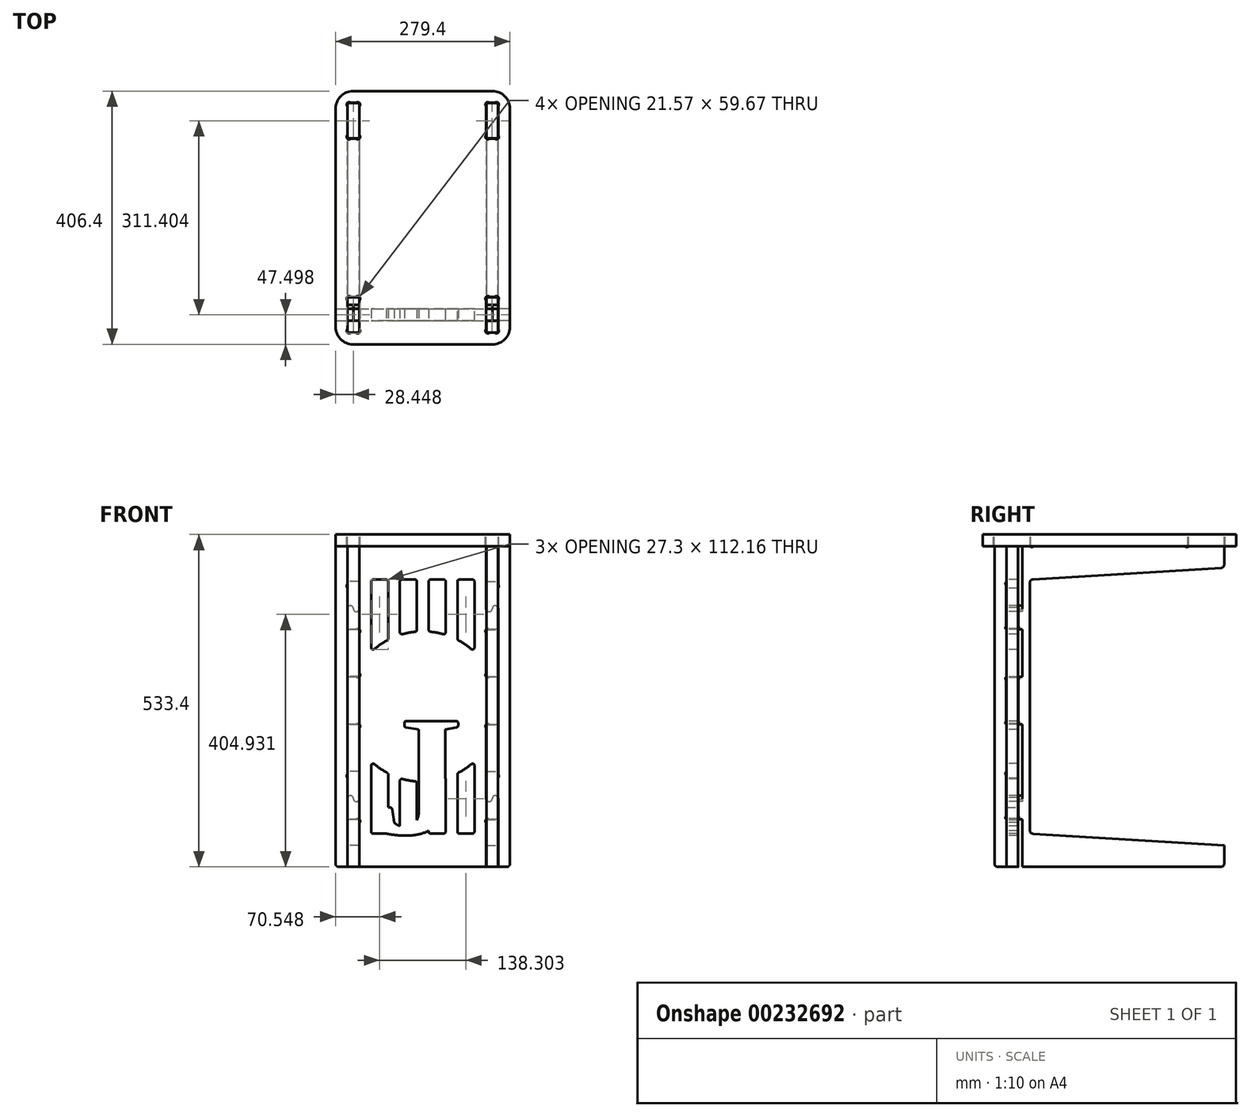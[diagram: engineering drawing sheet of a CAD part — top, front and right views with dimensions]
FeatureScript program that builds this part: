
annotation { "Feature Type Name" : "Feature", "Feature Type Description" : "" }
export const myFeature = defineFeature(function(context is Context, id is Id, definition is map)
    precondition{}
    {
        {
            assignVariable(context, id + "F0", {"name" : "table_width", "anyValue" : 279.4 * mm});
        }
        {
            assignVariable(context, id + "F1", {"name" : "material_thickness", "anyValue" : 18.8 * mm});
        }
        {
            assignVariable(context, id + "F2", {"name" : "material_clearance", "anyValue" : 0.25 * mm});
        }
        {
            assignVariable(context, id + "F3", {"name" : "tool_diameter", "anyValue" : 6.35 * mm});
        }
        {
            assignVariable(context, id + "F4", {"name" : "large_fillet_radius", "anyValue" : 0.1 * getVariable(context, 'table_width')});
        }
        {
            assignVariable(context, id + "F5", {"name" : "small_fillet_radius", "anyValue" : 0.25 * getVariable(context, 'material_thickness')});
        }
        {
            assignVariable(context, id + "F6", {"name" : "tabs_fillet_radius", "anyValue" : 0.1 * getVariable(context, 'material_thickness')});
        }
        {
            var Q0;
            Q0=qCreatedBy(makeId("Right.planeOp"),FACE);
            cPlane(context, id + "F7", {"entities" : qUnion([Q0]), "cplaneType" : CPlaneType.OFFSET, "offset" : getVariable(context, 'table_width') / 2 - getVariable(context, 'material_thickness') - getVariable(context, 'material_clearance'), "oppositeDirection" : true, "width" : 152.4 * mm, "height" : 152.4 * mm});
        }
        {
            var Q0;
            Q0=qCreatedBy(id+"F7.planeOp",FACE);
            var sketch = newSketch(context, id + "F8", { "sketchPlane" : qUnion([Q0])});
            skLineSegment(sketch, "E0.bottom", {"start": v(368.3, 0) * mm, "end": v(0, 0) * mm});
            skLineSegment(sketch, "E0.top", {"start": v(368.3, -533.4) * mm, "end": v(0, -533.4) * mm});
            skLineSegment(sketch, "E0.left", {"start": v(368.3, 0) * mm, "end": v(368.3, -533.4) * mm});
            skLineSegment(sketch, "E0.right", {"start": v(0, 0) * mm, "end": v(0, -533.4) * mm});
            skSolve(sketch);
        }
        {
            var Q0;
            Q0 = qSketchRegion(id + "F8", true);
            extrude(context, id + "F9", {"entities" : qUnion([Q0]), "depth" : getVariable(context, 'material_thickness')});
        }
        {
            var Q0;
            Q0=makeQuery(id+"F9.opExtrude","CAP_FACE",FACE,{"disambiguationData":[OSD([sQuery(id+"F8.wireOp",EDGE,"E0.bottom"),sQuery(id+"F8.wireOp",EDGE,"E0.top"),sQuery(id+"F8.wireOp",EDGE,"E0.left"),sQuery(id+"F8.wireOp",EDGE,"E0.right")])],"isStart":true});
            var sketch = newSketch(context, id + "F10", { "sketchPlane" : qUnion([Q0])});
            skLineSegment(sketch, "E1", {"start": v(-368.3, -53.34) * mm, "end": v(-56.9, -72.4) * mm});
            skLineSegment(sketch, "E2", {"start": v(-56.9, -72.4) * mm, "end": v(-56.9, -480.06) * mm});
            skLineSegment(sketch, "E3", {"start": v(-56.9, -480.06) * mm, "end": v(-368.3, -499.1) * mm});
            skLineSegment(sketch, "E4", {"start": v(-368.3, -499.1) * mm, "end": v(-368.3, -53.34) * mm});
            skLineSegment(sketch, "E5", {"start": v(-56.9, -72.4) * mm, "end": v(-368.3, -72.39) * mm, "construction": true});
            skLineSegment(sketch, "E6", {"start": v(-56.9, -480.06) * mm, "end": v(-368.3, -480.06) * mm, "construction": true});
            skLineSegment(sketch, "E7.bottom", {"start": v(-311.4, 0) * mm, "end": v(-56.9, 0) * mm});
            skLineSegment(sketch, "E7.top", {"start": v(-311.4, -19.05) * mm, "end": v(-56.9, -19.05) * mm});
            skLineSegment(sketch, "E7.left", {"start": v(-311.4, 0) * mm, "end": v(-311.4, -19.05) * mm});
            skLineSegment(sketch, "E7.right", {"start": v(-56.9, 0) * mm, "end": v(-56.9, -19.05) * mm});
            skLineSegment(sketch, "E8.bottom", {"start": v(-38.1, -75.95) * mm, "end": v(-18.8, -75.95) * mm});
            skLineSegment(sketch, "E8.top", {"start": v(-38.1, -152.65) * mm, "end": v(-18.8, -152.65) * mm});
            skLineSegment(sketch, "E8.left", {"start": v(-38.1, -75.95) * mm, "end": v(-38.1, -152.65) * mm});
            skLineSegment(sketch, "E8.right", {"start": v(-18.8, -75.95) * mm, "end": v(-18.8, -152.65) * mm});
            skLineSegment(sketch, "E9.0.1.0", {"start": v(-38.1, -305.05) * mm, "end": v(-18.8, -305.05) * mm});
            skLineSegment(sketch, "E9.0.1.1", {"start": v(-18.8, -228.35) * mm, "end": v(-18.8, -305.05) * mm});
            skLineSegment(sketch, "E9.0.1.2", {"start": v(-38.1, -228.35) * mm, "end": v(-38.1, -305.05) * mm});
            skLineSegment(sketch, "E9.0.1.3", {"start": v(-38.1, -228.35) * mm, "end": v(-18.8, -228.35) * mm});
            skLineSegment(sketch, "E9.0.2.0", {"start": v(-38.1, -457.45) * mm, "end": v(-18.8, -457.45) * mm});
            skLineSegment(sketch, "E9.0.2.1", {"start": v(-18.8, -380.75) * mm, "end": v(-18.8, -457.45) * mm});
            skLineSegment(sketch, "E9.0.2.2", {"start": v(-38.1, -380.75) * mm, "end": v(-38.1, -457.45) * mm});
            skLineSegment(sketch, "E9.0.2.3", {"start": v(-38.1, -380.75) * mm, "end": v(-18.8, -380.75) * mm});
            skLineSegment(sketch, "E9.direction1", {"start": v(-38.1, -152.65) * mm, "end": v(7.11, -152.65) * mm, "construction": true});
            skLineSegment(sketch, "E9.direction2", {"start": v(-38.1, -152.65) * mm, "end": v(-38.1, -305.05) * mm, "construction": true});
            skSolve(sketch);
        }
        {
            var Q0;
            Q0 = qSketchRegion(id + "F10", true);
            extrude(context, id + "F11", {"entities" : qUnion([Q0]), "operationType" : NewBodyOperationType.REMOVE, "oppositeDirection" : true, "depth" : getVariable(context, 'material_thickness')});
        }
        {
            var Q0;
            Q0=makeQuery(id+"F11.boolean.opBoolean","COPY",EDGE,{"derivedFrom":makeQuery(id+"F11.opExtrude","SWEPT_EDGE",EDGE,{"disambiguationData":[OSD([sQuery(id+"F8.wireOp",EDGE,"E0.left"),sQuery(id+"F10.wireOp",EDGE,"E1"),sQuery(id+"F10.wireOp",EDGE,"E4")])]})});
            var Q1;
            Q1=makeQuery(id+"F11.boolean.opBoolean","COPY",EDGE,{"derivedFrom":makeQuery(id+"F11.opExtrude","SWEPT_EDGE",EDGE,{"disambiguationData":[OSD([sQuery(id+"F10.wireOp",EDGE,"E1"),sQuery(id+"F10.wireOp",EDGE,"E2")])]})});
            var Q2;
            Q2=makeQuery(id+"F11.boolean.opBoolean","COPY",EDGE,{"derivedFrom":makeQuery(id+"F11.opExtrude","SWEPT_EDGE",EDGE,{"disambiguationData":[OSD([sQuery(id+"F10.wireOp",EDGE,"E2"),sQuery(id+"F10.wireOp",EDGE,"E3")])]})});
            var Q3;
            Q3=makeQuery(id+"F11.boolean.opBoolean","COPY",EDGE,{"derivedFrom":makeQuery(id+"F11.opExtrude","SWEPT_EDGE",EDGE,{"disambiguationData":[OSD([sQuery(id+"F8.wireOp",EDGE,"E0.left"),sQuery(id+"F10.wireOp",EDGE,"E3"),sQuery(id+"F10.wireOp",EDGE,"E4")])]})});
            var Q4;
            Q4=makeQuery(id+"F9.opExtrude","SWEPT_EDGE",EDGE,{"disambiguationData":[OSD([sQuery(id+"F8.wireOp",EDGE,"E0.top"),sQuery(id+"F8.wireOp",EDGE,"E0.left")])]});
            var Q5;
            Q5=makeQuery(id+"F9.opExtrude","SWEPT_EDGE",EDGE,{"disambiguationData":[OSD([sQuery(id+"F8.wireOp",EDGE,"E0.top"),sQuery(id+"F8.wireOp",EDGE,"E0.right")])]});
            fillet(context, id + "F12", {"entities" : qUnion([Q0, Q1, Q2, Q3, Q4, Q5]), "radius" : 5.08 * mm, "tangentPropagation" : true, "allowEdgeOverflow" : false});
        }
        {
            var Q0;
            Q0=makeQuery(id+"F9.opExtrude","SWEPT_EDGE",EDGE,{"disambiguationData":[OSD([sQuery(id+"F8.wireOp",EDGE,"E0.bottom"),sQuery(id+"F8.wireOp",EDGE,"E0.left")])]});
            var Q1;
            Q1=makeQuery(id+"F11.boolean.opBoolean","COPY",EDGE,{"derivedFrom":makeQuery(id+"F11.opExtrude","SWEPT_EDGE",EDGE,{"disambiguationData":[OSD([sQuery(id+"F8.wireOp",EDGE,"E0.bottom"),sQuery(id+"F10.wireOp",EDGE,"E7.bottom"),sQuery(id+"F10.wireOp",EDGE,"E7.left")])]})});
            var Q2;
            Q2=makeQuery(id+"F11.boolean.opBoolean","COPY",EDGE,{"derivedFrom":makeQuery(id+"F11.opExtrude","SWEPT_EDGE",EDGE,{"disambiguationData":[OSD([sQuery(id+"F8.wireOp",EDGE,"E0.bottom"),sQuery(id+"F10.wireOp",EDGE,"E7.bottom"),sQuery(id+"F10.wireOp",EDGE,"E7.right")])]})});
            var Q3;
            Q3=makeQuery(id+"F9.opExtrude","SWEPT_EDGE",EDGE,{"disambiguationData":[OSD([sQuery(id+"F8.wireOp",EDGE,"E0.bottom"),sQuery(id+"F8.wireOp",EDGE,"E0.right")])]});
            fillet(context, id + "F13", {"entities" : qUnion([Q0, Q1, Q2, Q3]), "radius" : getVariable(context, 'tabs_fillet_radius'), "tangentPropagation" : true, "allowEdgeOverflow" : false});
        }
        {
            var Q0;
            Q0=makeQuery(id+"F9.opExtrude","CAP_FACE",FACE,{"disambiguationData":[OSD([sQuery(id+"F8.wireOp",EDGE,"E0.bottom"),sQuery(id+"F8.wireOp",EDGE,"E0.top"),sQuery(id+"F8.wireOp",EDGE,"E0.left"),sQuery(id+"F8.wireOp",EDGE,"E0.right")])],"isStart":true});
            var sketch = newSketch(context, id + "F14", { "sketchPlane" : qUnion([Q0])});
            skArc(sketch, "E10", {"start": v(-311.99, -14.18) * mm, "mid": v(-311.4, -19.05) * mm, "end": v(-306.53, -19.63) * mm});
            skArc(sketch, "E11", {"start": v(-306.53, -19.63) * mm, "mid": v(-305.54, -19.2) * mm, "end": v(-304.46, -19.05) * mm});
            skArc(sketch, "E12", {"start": v(-311.99, -14.18) * mm, "mid": v(-311.55, -13.18) * mm, "end": v(-311.4, -12.1) * mm});
            skLineSegment(sketch, "E13", {"start": v(-308.6, -16.24) * mm, "end": v(-311.4, -19.05) * mm, "construction": true});
            skLineSegment(sketch, "E14", {"start": v(-184.15, -19.05) * mm, "end": v(-184.15, -64.6) * mm, "construction": true});
            skArc(sketch, "E15.MirrorCS", {"start": v(-56.31, -14.18) * mm, "mid": v(-56.75, -13.18) * mm, "end": v(-56.9, -12.1) * mm});
            skArc(sketch, "E16.MirrorCS", {"start": v(-56.31, -14.18) * mm, "mid": v(-56.9, -19.05) * mm, "end": v(-61.77, -19.63) * mm});
            skArc(sketch, "E17.MirrorCS", {"start": v(-61.77, -19.63) * mm, "mid": v(-62.76, -19.2) * mm, "end": v(-63.84, -19.05) * mm});
            skLineSegment(sketch, "E18", {"start": v(-311.4, -12.1) * mm, "end": v(-304.46, -19.05) * mm});
            skLineSegment(sketch, "E19.MirrorCS", {"start": v(-56.9, -12.1) * mm, "end": v(-63.84, -19.05) * mm});
            skLineSegment(sketch, "E20", {"start": v(-38.1, -114.3) * mm, "end": v(-18.8, -114.3) * mm, "construction": true});
            skLineSegment(sketch, "E21", {"start": v(-28.45, -75.95) * mm, "end": v(-28.45, -152.65) * mm, "construction": true});
            skArc(sketch, "E22", {"start": v(-33.23, -75.36) * mm, "mid": v(-38.1, -75.95) * mm, "end": v(-38.68, -80.82) * mm});
            skArc(sketch, "E23", {"start": v(-33.23, -75.36) * mm, "mid": v(-32.23, -75.8) * mm, "end": v(-31.16, -75.95) * mm});
            skArc(sketch, "E24", {"start": v(-38.68, -80.82) * mm, "mid": v(-38.25, -81.81) * mm, "end": v(-38.1, -82.89) * mm});
            skLineSegment(sketch, "E25", {"start": v(-35.3, -78.75) * mm, "end": v(-38.1, -75.95) * mm, "construction": true});
            skLineSegment(sketch, "E26", {"start": v(-38.1, -82.89) * mm, "end": v(-31.16, -75.95) * mm});
            skLineSegment(sketch, "E27.MirrorCS", {"start": v(-18.8, -82.89) * mm, "end": v(-25.74, -75.95) * mm});
            skArc(sketch, "E28.MirrorCS", {"start": v(-23.67, -75.36) * mm, "mid": v(-24.66, -75.8) * mm, "end": v(-25.74, -75.95) * mm});
            skArc(sketch, "E29.MirrorCS", {"start": v(-23.67, -75.36) * mm, "mid": v(-18.8, -75.95) * mm, "end": v(-18.21, -80.82) * mm});
            skArc(sketch, "E30.MirrorCS", {"start": v(-18.21, -80.82) * mm, "mid": v(-18.65, -81.81) * mm, "end": v(-18.8, -82.89) * mm});
            skLineSegment(sketch, "E31.MirrorCS", {"start": v(-38.1, -145.71) * mm, "end": v(-31.16, -152.65) * mm});
            skArc(sketch, "E32.MirrorCS", {"start": v(-38.68, -147.78) * mm, "mid": v(-38.25, -146.79) * mm, "end": v(-38.1, -145.71) * mm});
            skArc(sketch, "E33.MirrorCS", {"start": v(-33.23, -153.24) * mm, "mid": v(-38.1, -152.65) * mm, "end": v(-38.68, -147.78) * mm});
            skArc(sketch, "E34.MirrorCS", {"start": v(-33.23, -153.24) * mm, "mid": v(-32.23, -152.8) * mm, "end": v(-31.16, -152.65) * mm});
            skLineSegment(sketch, "E35.MirrorCS", {"start": v(-18.8, -145.71) * mm, "end": v(-25.74, -152.65) * mm});
            skArc(sketch, "E36.MirrorCS", {"start": v(-23.67, -153.24) * mm, "mid": v(-24.66, -152.8) * mm, "end": v(-25.74, -152.65) * mm});
            skArc(sketch, "E37.MirrorCS", {"start": v(-23.67, -153.24) * mm, "mid": v(-18.8, -152.65) * mm, "end": v(-18.21, -147.78) * mm});
            skArc(sketch, "E38.MirrorCS", {"start": v(-18.21, -147.78) * mm, "mid": v(-18.65, -146.79) * mm, "end": v(-18.8, -145.71) * mm});
            skArc(sketch, "E39.0.1.0", {"start": v(-38.68, -300.18) * mm, "mid": v(-38.25, -299.19) * mm, "end": v(-38.1, -298.11) * mm});
            skArc(sketch, "E39.0.1.1", {"start": v(-33.23, -305.64) * mm, "mid": v(-38.1, -305.05) * mm, "end": v(-38.68, -300.18) * mm});
            skArc(sketch, "E39.0.1.2", {"start": v(-33.23, -305.64) * mm, "mid": v(-32.23, -305.2) * mm, "end": v(-31.16, -305.05) * mm});
            skLineSegment(sketch, "E39.0.1.3", {"start": v(-38.1, -298.11) * mm, "end": v(-31.16, -305.05) * mm});
            skArc(sketch, "E39.0.1.4", {"start": v(-23.67, -305.64) * mm, "mid": v(-24.66, -305.2) * mm, "end": v(-25.74, -305.05) * mm});
            skLineSegment(sketch, "E39.0.1.5", {"start": v(-18.8, -298.11) * mm, "end": v(-25.74, -305.05) * mm});
            skArc(sketch, "E39.0.1.6", {"start": v(-23.67, -305.64) * mm, "mid": v(-18.8, -305.05) * mm, "end": v(-18.21, -300.18) * mm});
            skArc(sketch, "E39.0.1.7", {"start": v(-18.21, -300.18) * mm, "mid": v(-18.65, -299.19) * mm, "end": v(-18.8, -298.11) * mm});
            skLineSegment(sketch, "E39.0.1.8", {"start": v(-38.1, -235.29) * mm, "end": v(-31.16, -228.35) * mm});
            skArc(sketch, "E39.0.1.9", {"start": v(-33.23, -227.76) * mm, "mid": v(-32.23, -228.2) * mm, "end": v(-31.16, -228.35) * mm});
            skArc(sketch, "E39.0.1.10", {"start": v(-33.23, -227.76) * mm, "mid": v(-38.1, -228.35) * mm, "end": v(-38.68, -233.22) * mm});
            skArc(sketch, "E39.0.1.11", {"start": v(-38.68, -233.22) * mm, "mid": v(-38.25, -234.21) * mm, "end": v(-38.1, -235.29) * mm});
            skArc(sketch, "E39.0.1.12", {"start": v(-23.67, -227.76) * mm, "mid": v(-24.66, -228.2) * mm, "end": v(-25.74, -228.35) * mm});
            skArc(sketch, "E39.0.1.13", {"start": v(-23.67, -227.76) * mm, "mid": v(-18.8, -228.35) * mm, "end": v(-18.21, -233.22) * mm});
            skArc(sketch, "E39.0.1.14", {"start": v(-18.21, -233.22) * mm, "mid": v(-18.65, -234.21) * mm, "end": v(-18.8, -235.29) * mm});
            skLineSegment(sketch, "E39.0.1.15", {"start": v(-18.8, -235.29) * mm, "end": v(-25.74, -228.35) * mm});
            skArc(sketch, "E39.0.2.0", {"start": v(-38.68, -452.58) * mm, "mid": v(-38.25, -451.59) * mm, "end": v(-38.1, -450.51) * mm});
            skArc(sketch, "E39.0.2.1", {"start": v(-33.23, -458.04) * mm, "mid": v(-38.1, -457.45) * mm, "end": v(-38.68, -452.58) * mm});
            skArc(sketch, "E39.0.2.2", {"start": v(-33.23, -458.04) * mm, "mid": v(-32.23, -457.6) * mm, "end": v(-31.16, -457.45) * mm});
            skLineSegment(sketch, "E39.0.2.3", {"start": v(-38.1, -450.51) * mm, "end": v(-31.16, -457.45) * mm});
            skArc(sketch, "E39.0.2.4", {"start": v(-23.67, -458.04) * mm, "mid": v(-24.66, -457.6) * mm, "end": v(-25.74, -457.45) * mm});
            skLineSegment(sketch, "E39.0.2.5", {"start": v(-18.8, -450.51) * mm, "end": v(-25.74, -457.45) * mm});
            skArc(sketch, "E39.0.2.6", {"start": v(-23.67, -458.04) * mm, "mid": v(-18.8, -457.45) * mm, "end": v(-18.21, -452.58) * mm});
            skArc(sketch, "E39.0.2.7", {"start": v(-18.21, -452.58) * mm, "mid": v(-18.65, -451.59) * mm, "end": v(-18.8, -450.51) * mm});
            skLineSegment(sketch, "E39.0.2.8", {"start": v(-38.1, -387.69) * mm, "end": v(-31.16, -380.75) * mm});
            skArc(sketch, "E39.0.2.9", {"start": v(-33.23, -380.16) * mm, "mid": v(-32.23, -380.6) * mm, "end": v(-31.16, -380.75) * mm});
            skArc(sketch, "E39.0.2.10", {"start": v(-33.23, -380.16) * mm, "mid": v(-38.1, -380.75) * mm, "end": v(-38.68, -385.62) * mm});
            skArc(sketch, "E39.0.2.11", {"start": v(-38.68, -385.62) * mm, "mid": v(-38.25, -386.61) * mm, "end": v(-38.1, -387.69) * mm});
            skArc(sketch, "E39.0.2.12", {"start": v(-23.67, -380.16) * mm, "mid": v(-24.66, -380.6) * mm, "end": v(-25.74, -380.75) * mm});
            skArc(sketch, "E39.0.2.13", {"start": v(-23.67, -380.16) * mm, "mid": v(-18.8, -380.75) * mm, "end": v(-18.21, -385.62) * mm});
            skArc(sketch, "E39.0.2.14", {"start": v(-18.21, -385.62) * mm, "mid": v(-18.65, -386.61) * mm, "end": v(-18.8, -387.69) * mm});
            skLineSegment(sketch, "E39.0.2.15", {"start": v(-18.8, -387.69) * mm, "end": v(-25.74, -380.75) * mm});
            skLineSegment(sketch, "E39.direction1", {"start": v(-21.6, -149.85) * mm, "end": v(13.12, -149.28) * mm, "construction": true});
            skLineSegment(sketch, "E39.direction2", {"start": v(-21.6, -149.85) * mm, "end": v(-21.6, -302.25) * mm, "construction": true});
            skLineSegment(sketch, "E40", {"start": v(-21.6, -302.25) * mm, "end": v(-18.8, -305.05) * mm, "construction": true});
            skSolve(sketch);
        }
        {
            var Q0;
            Q0 = qSketchRegion(id + "F14", true);
            extrude(context, id + "F15", {"entities" : qUnion([Q0]), "operationType" : NewBodyOperationType.REMOVE, "oppositeDirection" : true, "depth" : getVariable(context, 'material_thickness')});
        }
        {
            var Q0;
            Q0=qCreatedBy(makeId("Front.planeOp"),FACE);
            cPlane(context, id + "F16", {"entities" : qUnion([Q0]), "cplaneType" : CPlaneType.OFFSET, "offset" : getVariable(context, 'material_thickness') + getVariable(context, 'material_clearance'), "oppositeDirection" : true, "width" : 152.4 * mm, "height" : 152.4 * mm});
        }
        {
            var Q0;
            Q0=qCreatedBy(id+"F16.planeOp",FACE);
            var sketch = newSketch(context, id + "F17", { "sketchPlane" : qUnion([Q0])});
            skLineSegment(sketch, "E41.bottom", {"start": v(-139.7, 0) * mm, "end": v(-101.85, 0) * mm});
            skLineSegment(sketch, "E41.top", {"start": v(-139.7, -533.4) * mm, "end": v(-101.85, -533.4) * mm});
            skLineSegment(sketch, "E41.left", {"start": v(-139.7, 0) * mm, "end": v(-139.7, -533.4) * mm});
            skLineSegment(sketch, "E41.right", {"start": v(-101.85, 0) * mm, "end": v(-101.85, -533.4) * mm});
            skSolve(sketch);
        }
        {
            var Q0;
            Q0 = qSketchRegion(id + "F17", true);
            extrude(context, id + "F18", {"entities" : qUnion([Q0]), "oppositeDirection" : true, "depth" : getVariable(context, 'material_thickness')});
        }
        {
            var Q0;
            Q0=makeQuery(id+"F18.opExtrude","CAP_FACE",FACE,{"disambiguationData":[OSD([sQuery(id+"F17.wireOp",EDGE,"E41.bottom"),sQuery(id+"F17.wireOp",EDGE,"E41.top"),sQuery(id+"F17.wireOp",EDGE,"E41.left"),sQuery(id+"F17.wireOp",EDGE,"E41.right")])],"isStart":true});
            var sketch = newSketch(context, id + "F19", { "sketchPlane" : qUnion([Q0])});
            skLineSegment(sketch, "E42.top", {"start": v(-101.85, -85.72) * mm, "end": v(-120.9, -85.72) * mm});
            skLineSegment(sketch, "E42.left", {"start": v(-101.85, 0) * mm, "end": v(-101.85, -85.72) * mm});
            skLineSegment(sketch, "E42.right", {"start": v(-120.9, -19.05) * mm, "end": v(-120.9, -85.72) * mm});
            skLineSegment(sketch, "E43", {"start": v(-120.9, -390.52) * mm, "end": v(-101.85, -390.52) * mm});
            skLineSegment(sketch, "E44", {"start": v(-101.85, -390.52) * mm, "end": v(-101.85, -119.06) * mm});
            skLineSegment(sketch, "E45", {"start": v(-120.9, -119.06) * mm, "end": v(-120.9, -390.52) * mm});
            skLineSegment(sketch, "E46", {"start": v(-120.9, -533.4) * mm, "end": v(-101.85, -533.4) * mm});
            skLineSegment(sketch, "E47", {"start": v(-101.85, -533.4) * mm, "end": v(-101.85, -423.86) * mm});
            skLineSegment(sketch, "E48", {"start": v(-120.9, -423.86) * mm, "end": v(-120.9, -533.4) * mm});
            skLineSegment(sketch, "E49", {"start": v(-120.65, -119.06) * mm, "end": v(-120.65, -152.4) * mm, "construction": true});
            skLineSegment(sketch, "E50", {"start": v(-120.65, -152.4) * mm, "end": v(-101.85, -152.4) * mm, "construction": true});
            skLineSegment(sketch, "E51", {"start": v(-101.85, -85.72) * mm, "end": v(-101.85, -119.06) * mm, "construction": true});
            skLineSegment(sketch, "E52", {"start": v(-101.85, -390.52) * mm, "end": v(-101.85, -423.86) * mm, "construction": true});
            skLineSegment(sketch, "E53.bottom", {"start": v(-139.7, 0) * mm, "end": v(-101.85, 0) * mm});
            skLineSegment(sketch, "E53.left", {"start": v(-139.7, 0) * mm, "end": v(-139.7, -19.05) * mm});
            skLineSegment(sketch, "E54", {"start": v(-139.7, -19.05) * mm, "end": v(-120.9, -19.05) * mm});
            skArc(sketch, "E55", {"start": v(-120.9, -119.06) * mm, "mid": v(-116.01, -114.17) * mm, "end": v(-111.12, -119.06) * mm});
            skArc(sketch, "E56", {"start": v(-111.12, -119.06) * mm, "mid": v(-106.49, -123.7) * mm, "end": v(-101.85, -119.06) * mm});
            skArc(sketch, "E57", {"start": v(-120.65, -119.06) * mm, "mid": v(-116.01, -114.43) * mm, "end": v(-111.38, -119.06) * mm, "construction": true});
            skArc(sketch, "E58", {"start": v(-111.38, -119.06) * mm, "mid": v(-106.49, -123.95) * mm, "end": v(-101.6, -119.06) * mm, "construction": true});
            skPoint(sketch, "E59", {"position": v(-106.49, -123.7) * mm});
            skArc(sketch, "E60", {"start": v(-120.9, -423.86) * mm, "mid": v(-116.01, -418.97) * mm, "end": v(-111.12, -423.86) * mm});
            skArc(sketch, "E61", {"start": v(-111.12, -423.86) * mm, "mid": v(-106.49, -428.5) * mm, "end": v(-101.85, -423.86) * mm});
            skArc(sketch, "E62", {"start": v(-120.65, -423.86) * mm, "mid": v(-116.01, -419.23) * mm, "end": v(-111.38, -423.86) * mm, "construction": true});
            skLineSegment(sketch, "E63", {"start": v(-120.65, -423.86) * mm, "end": v(-120.65, -457.2) * mm, "construction": true});
            skSolve(sketch);
        }
        {
            var Q0;
            Q0 = qSketchRegion(id + "F19", true);
            extrude(context, id + "F20", {"entities" : qUnion([Q0]), "operationType" : NewBodyOperationType.REMOVE, "oppositeDirection" : true, "depth" : getVariable(context, 'material_thickness')});
        }
        {
            var Q0;
            Q0=makeQuery(id+"F20.boolean.opBoolean","COPY",EDGE,{"derivedFrom":makeQuery(id+"F20.opExtrude","SWEPT_EDGE",EDGE,{"disambiguationData":[OSD([sQuery(id+"F17.wireOp",EDGE,"E41.right"),sQuery(id+"F19.wireOp",EDGE,"E42.top"),sQuery(id+"F19.wireOp",EDGE,"E42.left")])]})});
            var Q1;
            Q1=makeQuery(id+"F20.boolean.opBoolean","COPY",EDGE,{"derivedFrom":makeQuery(id+"F20.opExtrude","SWEPT_EDGE",EDGE,{"disambiguationData":[OSD([sQuery(id+"F17.wireOp",EDGE,"E41.right"),sQuery(id+"F19.wireOp",EDGE,"E43"),sQuery(id+"F19.wireOp",EDGE,"E44")])]})});
            fillet(context, id + "F21", {"entities" : qUnion([Q0, Q1]), "radius" : getVariable(context, 'tabs_fillet_radius'), "tangentPropagation" : true, "allowEdgeOverflow" : false});
        }
        {
            var Q0;
            Q0=makeQuery(id+"F18.opExtrude","SWEPT_EDGE",EDGE,{"disambiguationData":[OSD([sQuery(id+"F17.wireOp",EDGE,"E41.top"),sQuery(id+"F17.wireOp",EDGE,"E41.left")])]});
            fillet(context, id + "F22", {"entities" : qUnion([Q0]), "radius" : getVariable(context, 'small_fillet_radius'), "tangentPropagation" : true, "allowEdgeOverflow" : false});
        }
        {
            var Q0;
            Q0=makeQuery(id+"F18.opExtrude","CAP_FACE",FACE,{"disambiguationData":[OSD([sQuery(id+"F17.wireOp",EDGE,"E41.bottom"),sQuery(id+"F17.wireOp",EDGE,"E41.top"),sQuery(id+"F17.wireOp",EDGE,"E41.left"),sQuery(id+"F17.wireOp",EDGE,"E41.right")])],"isStart":true});
            var sketch = newSketch(context, id + "F23", { "sketchPlane" : qUnion([Q0])});
            skArc(sketch, "E64", {"start": v(-121.49, -80.85) * mm, "mid": v(-120.9, -85.72) * mm, "end": v(-116.03, -86.3) * mm});
            skArc(sketch, "E65", {"start": v(-116.03, -86.3) * mm, "mid": v(-115.04, -85.87) * mm, "end": v(-113.96, -85.72) * mm});
            skArc(sketch, "E66", {"start": v(-121.49, -80.85) * mm, "mid": v(-121.05, -79.86) * mm, "end": v(-120.9, -78.78) * mm});
            skLineSegment(sketch, "E67", {"start": v(-120.9, -78.78) * mm, "end": v(-113.96, -85.72) * mm});
            skLineSegment(sketch, "E68", {"start": v(-120.9, -85.72) * mm, "end": v(-118.1, -82.92) * mm, "construction": true});
            skLineSegment(sketch, "E69.0.1.0", {"start": v(-120.9, -383.58) * mm, "end": v(-113.96, -390.52) * mm});
            skArc(sketch, "E69.0.1.1", {"start": v(-121.49, -385.65) * mm, "mid": v(-121.05, -384.66) * mm, "end": v(-120.9, -383.58) * mm});
            skArc(sketch, "E69.0.1.2", {"start": v(-121.49, -385.65) * mm, "mid": v(-120.9, -390.52) * mm, "end": v(-116.03, -391.1) * mm});
            skArc(sketch, "E69.0.1.3", {"start": v(-116.03, -391.1) * mm, "mid": v(-115.04, -390.67) * mm, "end": v(-113.96, -390.52) * mm});
            skLineSegment(sketch, "E70", {"start": v(-120.9, -390.52) * mm, "end": v(-118.1, -387.72) * mm, "construction": true});
            skSolve(sketch);
        }
        {
            var Q0;
            Q0 = qSketchRegion(id + "F23", true);
            extrude(context, id + "F24", {"entities" : qUnion([Q0]), "operationType" : NewBodyOperationType.REMOVE, "oppositeDirection" : true, "depth" : getVariable(context, 'material_thickness')});
        }
        {
            var Q0;
            Q0=makeQuery(id+"F18.opExtrude","SWEPT_BODY",BODY,{"disambiguationData":[OSD([sQuery(id+"F17.wireOp",EDGE,"E41.bottom"),sQuery(id+"F17.wireOp",EDGE,"E41.top"),sQuery(id+"F17.wireOp",EDGE,"E41.left"),sQuery(id+"F17.wireOp",EDGE,"E41.right")])]});
            var Q1;
            Q1=qCreatedBy(makeId("Right.planeOp"),FACE);
            mirror(context, id + "F25", {"entities" : qUnion([Q0]), "mirrorPlane" : qUnion([Q1])});
        }
        {
            var Q0;
            Q0=qCreatedBy(makeId("Front.planeOp"),FACE);
            cPlane(context, id + "F26", {"entities" : qUnion([Q0]), "cplaneType" : CPlaneType.OFFSET, "offset" : getVariable(context, 'material_thickness') + getVariable(context, 'material_clearance'), "oppositeDirection" : true, "width" : 152.4 * mm, "height" : 152.4 * mm});
        }
        {
            var Q0;
            Q0=qCreatedBy(id+"F26.planeOp",FACE);
            var sketch = newSketch(context, id + "F27", { "sketchPlane" : qUnion([Q0])});
            skLineSegment(sketch, "E71.bottom", {"start": v(-120.65, 0) * mm, "end": v(120.65, 0) * mm});
            skLineSegment(sketch, "E71.top", {"start": v(-120.65, -533.4) * mm, "end": v(120.65, -533.4) * mm});
            skLineSegment(sketch, "E71.left", {"start": v(-120.65, 0) * mm, "end": v(-120.65, -533.4) * mm});
            skLineSegment(sketch, "E71.right", {"start": v(120.65, 0) * mm, "end": v(120.65, -533.4) * mm});
            skPoint(sketch, "E72", {"position": v(0, 0) * mm});
            skSolve(sketch);
        }
        {
            var Q0;
            Q0 = qSketchRegion(id + "F27", true);
            extrude(context, id + "F28", {"entities" : qUnion([Q0]), "oppositeDirection" : true, "depth" : getVariable(context, 'material_thickness')});
        }
        {
            var Q0;
            Q0=makeQuery(id+"F28.opExtrude","CAP_FACE",FACE,{"disambiguationData":[OSD([sQuery(id+"F27.wireOp",EDGE,"E71.bottom"),sQuery(id+"F27.wireOp",EDGE,"E71.top"),sQuery(id+"F27.wireOp",EDGE,"E71.left"),sQuery(id+"F27.wireOp",EDGE,"E71.right")])],"isStart":true});
            var sketch = newSketch(context, id + "F29", { "sketchPlane" : qUnion([Q0])});
            skLineSegment(sketch, "E73", {"start": v(-101.6, -119.06) * mm, "end": v(-101.6, -19.05) * mm});
            skLineSegment(sketch, "E74", {"start": v(-101.6, -19.05) * mm, "end": v(101.6, -19.05) * mm});
            skLineSegment(sketch, "E75", {"start": v(101.6, -19.05) * mm, "end": v(101.6, -119.06) * mm});
            skLineSegment(sketch, "E76", {"start": v(120.65, -119.06) * mm, "end": v(120.65, 0) * mm});
            skLineSegment(sketch, "E77", {"start": v(120.65, 0) * mm, "end": v(-120.65, 0) * mm});
            skLineSegment(sketch, "E78", {"start": v(-120.65, 0) * mm, "end": v(-120.65, -119.06) * mm});
            skLineSegment(sketch, "E79", {"start": v(-120.65, -152.4) * mm, "end": v(-101.6, -152.4) * mm});
            skLineSegment(sketch, "E80", {"start": v(120.65, -152.4) * mm, "end": v(101.6, -152.4) * mm});
            skLineSegment(sketch, "E81", {"start": v(-120.65, -457.2) * mm, "end": v(-101.6, -457.2) * mm});
            skLineSegment(sketch, "E82", {"start": v(-101.6, -457.2) * mm, "end": v(-101.6, -533.4) * mm});
            skLineSegment(sketch, "E83", {"start": v(-101.6, -533.4) * mm, "end": v(-120.65, -533.4) * mm});
            skLineSegment(sketch, "E84", {"start": v(-120.65, -533.4) * mm, "end": v(-120.65, -457.2) * mm});
            skLineSegment(sketch, "E85", {"start": v(120.65, -457.2) * mm, "end": v(101.6, -457.2) * mm});
            skLineSegment(sketch, "E86", {"start": v(101.6, -457.2) * mm, "end": v(101.6, -533.4) * mm});
            skLineSegment(sketch, "E87", {"start": v(101.6, -533.4) * mm, "end": v(120.65, -533.4) * mm});
            skLineSegment(sketch, "E88", {"start": v(120.65, -533.4) * mm, "end": v(120.65, -457.2) * mm});
            skLineSegment(sketch, "E89", {"start": v(-120.65, -119.06) * mm, "end": v(-120.65, -152.4) * mm, "construction": true});
            skLineSegment(sketch, "E90", {"start": v(120.65, -119.06) * mm, "end": v(120.65, -152.4) * mm, "construction": true});
            skLineSegment(sketch, "E91", {"start": v(-120.65, -423.86) * mm, "end": v(-120.65, -457.2) * mm, "construction": true});
            skLineSegment(sketch, "E92", {"start": v(120.65, -423.86) * mm, "end": v(120.65, -457.2) * mm, "construction": true});
            skLineSegment(sketch, "E93", {"start": v(101.6, -152.4) * mm, "end": v(101.6, -228.6) * mm});
            skLineSegment(sketch, "E94", {"start": v(101.6, -228.6) * mm, "end": v(120.65, -228.6) * mm});
            skLineSegment(sketch, "E95", {"start": v(120.65, -228.6) * mm, "end": v(120.65, -152.4) * mm});
            skLineSegment(sketch, "E96", {"start": v(-120.65, -152.4) * mm, "end": v(-120.65, -228.6) * mm});
            skLineSegment(sketch, "E97", {"start": v(-120.65, -228.6) * mm, "end": v(-101.6, -228.6) * mm});
            skLineSegment(sketch, "E98", {"start": v(-101.6, -228.6) * mm, "end": v(-101.6, -152.4) * mm});
            skLineSegment(sketch, "E99", {"start": v(-101.6, -423.86) * mm, "end": v(-101.6, -304.8) * mm});
            skLineSegment(sketch, "E100", {"start": v(-101.6, -304.8) * mm, "end": v(-120.65, -304.8) * mm});
            skLineSegment(sketch, "E101", {"start": v(-120.65, -304.8) * mm, "end": v(-120.65, -423.86) * mm});
            skLineSegment(sketch, "E102", {"start": v(101.6, -423.86) * mm, "end": v(101.6, -304.8) * mm});
            skLineSegment(sketch, "E103", {"start": v(101.6, -304.8) * mm, "end": v(120.65, -304.8) * mm});
            skLineSegment(sketch, "E104", {"start": v(120.65, -304.8) * mm, "end": v(120.65, -423.86) * mm});
            skArc(sketch, "E105", {"start": v(-120.65, -119.06) * mm, "mid": v(-116.01, -114.43) * mm, "end": v(-111.38, -119.06) * mm});
            skArc(sketch, "E106", {"start": v(-111.38, -119.06) * mm, "mid": v(-106.49, -123.95) * mm, "end": v(-101.6, -119.06) * mm});
            skPoint(sketch, "E107", {"position": v(-116.01, -114.43) * mm});
            skArc(sketch, "E108.MirrorCS", {"start": v(111.38, -119.06) * mm, "mid": v(106.49, -123.95) * mm, "end": v(101.6, -119.06) * mm});
            skArc(sketch, "E109.MirrorCS", {"start": v(120.65, -119.06) * mm, "mid": v(116.01, -114.43) * mm, "end": v(111.38, -119.06) * mm});
            skArc(sketch, "E110", {"start": v(-120.65, -423.86) * mm, "mid": v(-116.01, -419.23) * mm, "end": v(-111.38, -423.86) * mm});
            skArc(sketch, "E111", {"start": v(-101.6, -423.86) * mm, "mid": v(-106.49, -428.75) * mm, "end": v(-111.38, -423.86) * mm});
            skArc(sketch, "E112.MirrorCS", {"start": v(101.6, -423.86) * mm, "mid": v(106.49, -428.75) * mm, "end": v(111.38, -423.86) * mm});
            skArc(sketch, "E113.MirrorCS", {"start": v(120.65, -423.86) * mm, "mid": v(116.01, -419.23) * mm, "end": v(111.38, -423.86) * mm});
            skPoint(sketch, "E114", {"position": v(-106.49, -123.95) * mm});
            skSolve(sketch);
        }
        {
            var Q0;
            Q0 = qSketchRegion(id + "F29", true);
            extrude(context, id + "F30", {"entities" : qUnion([Q0]), "operationType" : NewBodyOperationType.REMOVE, "oppositeDirection" : true, "depth" : 25.4 * mm});
        }
        {
            var Q0;
            Q0=makeQuery(id+"F28.opExtrude","CAP_FACE",FACE,{"disambiguationData":[OSD([sQuery(id+"F27.wireOp",EDGE,"E71.bottom"),sQuery(id+"F27.wireOp",EDGE,"E71.top"),sQuery(id+"F27.wireOp",EDGE,"E71.left"),sQuery(id+"F27.wireOp",EDGE,"E71.right")])],"isStart":true});
            var sketch = newSketch(context, id + "F31", { "sketchPlane" : qUnion([Q0])});
            skPoint(sketch, "E115", {"position": v(-120.65, -266.7) * mm});
            skPoint(sketch, "E116", {"position": v(120.65, -266.7) * mm});
            skLineSegment(sketch, "E117", {"start": v(-120.65, -276.23) * mm, "end": v(120.65, -276.23) * mm, "construction": true});
            skPoint(sketch, "E118", {"position": v(0, -276.23) * mm});
            skCircle(sketch, "E119", {"center": v(0, -276.23) * mm, "radius": 120.65 * mm, "construction": true});
            skLineSegment(sketch, "E120", {"start": v(-101.6, -72.4) * mm, "end": v(101.6, -72.4) * mm, "construction": true});
            skLineSegment(sketch, "E121", {"start": v(-101.6, -480.06) * mm, "end": v(101.6, -480.06) * mm, "construction": true});
            skLineSegment(sketch, "E122", {"start": v(0, -276.23) * mm, "end": v(0, -72.4) * mm, "construction": true});
            skArc(sketch, "E123", {"start": v(-82.8, -188.48) * mm, "mid": v(-69.83, -177.83) * mm, "end": v(-55.5, -169.1) * mm});
            skArc(sketch, "E124", {"start": v(-36.7, -161.3) * mm, "mid": v(-23.2, -157.83) * mm, "end": v(-9.4, -155.94) * mm});
            skLineSegment(sketch, "E125", {"start": v(-82.8, -188.48) * mm, "end": v(-82.8, -72.4) * mm});
            skLineSegment(sketch, "E126", {"start": v(-82.8, -72.4) * mm, "end": v(-55.5, -72.4) * mm});
            skLineSegment(sketch, "E127", {"start": v(-55.5, -72.4) * mm, "end": v(-55.5, -169.1) * mm});
            skLineSegment(sketch, "E128", {"start": v(-36.7, -161.3) * mm, "end": v(-36.7, -72.4) * mm});
            skLineSegment(sketch, "E129", {"start": v(-36.7, -72.4) * mm, "end": v(-9.4, -72.4) * mm});
            skLineSegment(sketch, "E130", {"start": v(-9.4, -72.4) * mm, "end": v(-9.4, -155.94) * mm});
            skLineSegment(sketch, "E131", {"start": v(-82.8, -72.4) * mm, "end": v(-101.6, -72.4) * mm, "construction": true});
            skLineSegment(sketch, "E132", {"start": v(-55.5, -72.4) * mm, "end": v(-36.7, -72.4) * mm, "construction": true});
            skLineSegment(sketch, "E133", {"start": v(-9.4, -72.4) * mm, "end": v(9.4, -72.4) * mm, "construction": true});
            skLineSegment(sketch, "E134", {"start": v(9.4, -72.4) * mm, "end": v(36.7, -72.4) * mm, "construction": true});
            skLineSegment(sketch, "E135", {"start": v(36.7, -72.4) * mm, "end": v(55.5, -72.4) * mm, "construction": true});
            skLineSegment(sketch, "E136", {"start": v(55.5, -72.4) * mm, "end": v(82.8, -72.4) * mm, "construction": true});
            skLineSegment(sketch, "E137", {"start": v(82.8, -72.4) * mm, "end": v(101.6, -72.4) * mm, "construction": true});
            skLineSegment(sketch, "E138.MirrorCS", {"start": v(36.7, -72.4) * mm, "end": v(9.4, -72.4) * mm});
            skLineSegment(sketch, "E139.MirrorCS", {"start": v(82.8, -72.4) * mm, "end": v(55.5, -72.4) * mm});
            skLineSegment(sketch, "E140.MirrorCS", {"start": v(9.4, -72.4) * mm, "end": v(9.4, -155.94) * mm});
            skLineSegment(sketch, "E141.MirrorCS", {"start": v(36.7, -161.3) * mm, "end": v(36.7, -72.4) * mm});
            skLineSegment(sketch, "E142.MirrorCS", {"start": v(55.5, -72.4) * mm, "end": v(55.5, -169.1) * mm});
            skLineSegment(sketch, "E143.MirrorCS", {"start": v(82.8, -188.48) * mm, "end": v(82.8, -72.4) * mm});
            skArc(sketch, "E144.MirrorCS", {"start": v(82.8, -188.48) * mm, "mid": v(69.83, -177.83) * mm, "end": v(55.5, -169.1) * mm});
            skArc(sketch, "E145.MirrorCS", {"start": v(36.7, -161.3) * mm, "mid": v(23.2, -157.83) * mm, "end": v(9.4, -155.94) * mm});
            skArc(sketch, "E146.MirrorCS", {"start": v(82.8, -363.97) * mm, "mid": v(69.83, -374.62) * mm, "end": v(55.5, -383.35) * mm});
            skArc(sketch, "E147.MirrorCS", {"start": v(36.7, -391.16) * mm, "mid": v(23.2, -394.62) * mm, "end": v(9.4, -396.5) * mm});
            skArc(sketch, "E148.MirrorCS", {"start": v(-36.7, -391.16) * mm, "mid": v(-23.2, -394.62) * mm, "end": v(-9.4, -396.5) * mm});
            skArc(sketch, "E149.MirrorCS", {"start": v(-82.8, -363.97) * mm, "mid": v(-69.83, -374.62) * mm, "end": v(-55.5, -383.35) * mm});
            skLineSegment(sketch, "E150.MirrorCS", {"start": v(-82.8, -363.97) * mm, "end": v(-82.8, -480.06) * mm});
            skLineSegment(sketch, "E151.MirrorCS", {"start": v(-55.5, -480.06) * mm, "end": v(-55.5, -383.35) * mm});
            skLineSegment(sketch, "E152.MirrorCS", {"start": v(-36.7, -391.16) * mm, "end": v(-36.7, -480.06) * mm});
            skLineSegment(sketch, "E153.MirrorCS", {"start": v(-9.4, -480.06) * mm, "end": v(-9.4, -396.5) * mm});
            skLineSegment(sketch, "E154.MirrorCS", {"start": v(9.4, -480.06) * mm, "end": v(9.4, -396.5) * mm});
            skLineSegment(sketch, "E155.MirrorCS", {"start": v(36.7, -391.16) * mm, "end": v(36.7, -480.06) * mm});
            skLineSegment(sketch, "E156.MirrorCS", {"start": v(55.5, -480.06) * mm, "end": v(55.5, -383.35) * mm});
            skLineSegment(sketch, "E157.MirrorCS", {"start": v(82.8, -363.97) * mm, "end": v(82.8, -480.06) * mm});
            skLineSegment(sketch, "E158.MirrorCS", {"start": v(82.8, -480.06) * mm, "end": v(55.5, -480.06) * mm});
            skLineSegment(sketch, "E159.MirrorCS", {"start": v(9.4, -480.06) * mm, "end": v(36.7, -480.06) * mm, "construction": true});
            skLineSegment(sketch, "E160.MirrorCS", {"start": v(55.5, -480.06) * mm, "end": v(82.8, -480.06) * mm, "construction": true});
            skLineSegment(sketch, "E161.MirrorCS", {"start": v(36.7, -480.06) * mm, "end": v(9.4, -480.06) * mm});
            skLineSegment(sketch, "E162.MirrorCS", {"start": v(-36.7, -480.06) * mm, "end": v(-9.4, -480.06) * mm});
            skLineSegment(sketch, "E163.MirrorCS", {"start": v(-82.8, -480.06) * mm, "end": v(-55.5, -480.06) * mm});
            skSolve(sketch);
        }
        {
            var Q0;
            Q0 = qSketchRegion(id + "F31", true);
            extrude(context, id + "F32", {"entities" : qUnion([Q0]), "operationType" : NewBodyOperationType.REMOVE, "oppositeDirection" : true, "depth" : getVariable(context, 'material_thickness')});
        }
        {
            var Q0;
            Q0=makeQuery(id+"F28.opExtrude","CAP_FACE",FACE,{"disambiguationData":[OSD([sQuery(id+"F27.wireOp",EDGE,"E71.bottom"),sQuery(id+"F27.wireOp",EDGE,"E71.top"),sQuery(id+"F27.wireOp",EDGE,"E71.left"),sQuery(id+"F27.wireOp",EDGE,"E71.right")])],"isStart":true});
            var sketch = newSketch(context, id + "F33", { "sketchPlane" : qUnion([Q0])});
            skCircle(sketch, "E164", {"center": v(0, -276.23) * mm, "radius": 120.65 * mm, "construction": true});
            skText(sketch, "E165", { "text": "J", "fontName": "Tinos-Bold.ttf"});
            skLineSegment(sketch, "E166", {"start": v(-74.04, -167.09) * mm, "end": v(-120.65, -266.7) * mm, "construction": true});
            skLineSegment(sketch, "E167", {"start": v(-120.65, -266.7) * mm, "end": v(-74.04, -366.31) * mm, "construction": true});
            const initialGuessF33  = {"E165": [-0.07404, -0.48061, 1, 0, 0.19923]};
            skSetInitialGuess(sketch, initialGuessF33);
            skSolve(sketch);
        }
        {
            var Q0;
            Q0 = qSketchRegion(id + "F33", true);
            extrude(context, id + "F34", {"entities" : qUnion([Q0]), "operationType" : NewBodyOperationType.REMOVE, "oppositeDirection" : true, "depth" : getVariable(context, 'material_thickness')});
        }
        {
            var Q0;
            Q0=makeQuery(id+"F32.boolean.opBoolean","COPY",EDGE,{"derivedFrom":makeQuery(id+"F32.opExtrude","SWEPT_EDGE",EDGE,{"disambiguationData":[OSD([sQuery(id+"F31.wireOp",EDGE,"E123"),sQuery(id+"F31.wireOp",EDGE,"E125")])]})});
            var Q1;
            Q1=makeQuery(id+"F32.boolean.opBoolean","COPY",EDGE,{"derivedFrom":makeQuery(id+"F32.opExtrude","SWEPT_EDGE",EDGE,{"disambiguationData":[OSD([sQuery(id+"F31.wireOp",EDGE,"E124"),sQuery(id+"F31.wireOp",EDGE,"E128")])]})});
            var Q2;
            Q2=makeQuery(id+"F32.boolean.opBoolean","COPY",EDGE,{"derivedFrom":makeQuery(id+"F32.opExtrude","SWEPT_EDGE",EDGE,{"disambiguationData":[OSD([sQuery(id+"F31.wireOp",EDGE,"E140.MirrorCS"),sQuery(id+"F31.wireOp",EDGE,"E145.MirrorCS")])]})});
            var Q3;
            Q3=makeQuery(id+"F32.boolean.opBoolean","COPY",EDGE,{"derivedFrom":makeQuery(id+"F32.opExtrude","SWEPT_EDGE",EDGE,{"disambiguationData":[OSD([sQuery(id+"F31.wireOp",EDGE,"E142.MirrorCS"),sQuery(id+"F31.wireOp",EDGE,"E144.MirrorCS")])]})});
            var Q4;
            Q4=makeQuery(id+"F32.boolean.opBoolean","COPY",EDGE,{"derivedFrom":makeQuery(id+"F32.opExtrude","SWEPT_EDGE",EDGE,{"disambiguationData":[OSD([sQuery(id+"F31.wireOp",EDGE,"E143.MirrorCS"),sQuery(id+"F31.wireOp",EDGE,"E144.MirrorCS")])]})});
            var Q5;
            Q5=makeQuery(id+"F32.boolean.opBoolean","COPY",EDGE,{"derivedFrom":makeQuery(id+"F32.opExtrude","SWEPT_EDGE",EDGE,{"disambiguationData":[OSD([sQuery(id+"F31.wireOp",EDGE,"E141.MirrorCS"),sQuery(id+"F31.wireOp",EDGE,"E145.MirrorCS")])]})});
            var Q6;
            Q6=makeQuery(id+"F32.boolean.opBoolean","COPY",EDGE,{"derivedFrom":makeQuery(id+"F32.opExtrude","SWEPT_EDGE",EDGE,{"disambiguationData":[OSD([sQuery(id+"F31.wireOp",EDGE,"E124"),sQuery(id+"F31.wireOp",EDGE,"E130")])]})});
            var Q7;
            Q7=makeQuery(id+"F32.boolean.opBoolean","COPY",EDGE,{"derivedFrom":makeQuery(id+"F32.opExtrude","SWEPT_EDGE",EDGE,{"disambiguationData":[OSD([sQuery(id+"F31.wireOp",EDGE,"E123"),sQuery(id+"F31.wireOp",EDGE,"E127")])]})});
            var Q8;
            Q8=makeQuery(id+"F32.boolean.opBoolean","COPY",EDGE,{"derivedFrom":makeQuery(id+"F32.opExtrude","SWEPT_EDGE",EDGE,{"disambiguationData":[OSD([sQuery(id+"F31.wireOp",EDGE,"E125"),sQuery(id+"F31.wireOp",EDGE,"E126")])]})});
            var Q9;
            Q9=makeQuery(id+"F32.boolean.opBoolean","COPY",EDGE,{"derivedFrom":makeQuery(id+"F32.opExtrude","SWEPT_EDGE",EDGE,{"disambiguationData":[OSD([sQuery(id+"F31.wireOp",EDGE,"E128"),sQuery(id+"F31.wireOp",EDGE,"E129")])]})});
            var Q10;
            Q10=makeQuery(id+"F32.boolean.opBoolean","COPY",EDGE,{"derivedFrom":makeQuery(id+"F32.opExtrude","SWEPT_EDGE",EDGE,{"disambiguationData":[OSD([sQuery(id+"F31.wireOp",EDGE,"E138.MirrorCS"),sQuery(id+"F31.wireOp",EDGE,"E140.MirrorCS")])]})});
            var Q11;
            Q11=makeQuery(id+"F32.boolean.opBoolean","COPY",EDGE,{"derivedFrom":makeQuery(id+"F32.opExtrude","SWEPT_EDGE",EDGE,{"disambiguationData":[OSD([sQuery(id+"F31.wireOp",EDGE,"E139.MirrorCS"),sQuery(id+"F31.wireOp",EDGE,"E142.MirrorCS")])]})});
            var Q12;
            Q12=makeQuery(id+"F32.boolean.opBoolean","COPY",EDGE,{"derivedFrom":makeQuery(id+"F32.opExtrude","SWEPT_EDGE",EDGE,{"disambiguationData":[OSD([sQuery(id+"F31.wireOp",EDGE,"E139.MirrorCS"),sQuery(id+"F31.wireOp",EDGE,"E143.MirrorCS")])]})});
            var Q13;
            Q13=makeQuery(id+"F32.boolean.opBoolean","COPY",EDGE,{"derivedFrom":makeQuery(id+"F32.opExtrude","SWEPT_EDGE",EDGE,{"disambiguationData":[OSD([sQuery(id+"F31.wireOp",EDGE,"E138.MirrorCS"),sQuery(id+"F31.wireOp",EDGE,"E141.MirrorCS")])]})});
            var Q14;
            Q14=makeQuery(id+"F32.boolean.opBoolean","COPY",EDGE,{"derivedFrom":makeQuery(id+"F32.opExtrude","SWEPT_EDGE",EDGE,{"disambiguationData":[OSD([sQuery(id+"F31.wireOp",EDGE,"E129"),sQuery(id+"F31.wireOp",EDGE,"E130")])]})});
            var Q15;
            Q15=makeQuery(id+"F32.boolean.opBoolean","COPY",EDGE,{"derivedFrom":makeQuery(id+"F32.opExtrude","SWEPT_EDGE",EDGE,{"disambiguationData":[OSD([sQuery(id+"F31.wireOp",EDGE,"E126"),sQuery(id+"F31.wireOp",EDGE,"E127")])]})});
            var Q16;
            Q16=makeQuery(id+"F32.boolean.opBoolean","COPY",EDGE,{"derivedFrom":makeQuery(id+"F32.opExtrude","SWEPT_EDGE",EDGE,{"disambiguationData":[OSD([sQuery(id+"F31.wireOp",EDGE,"E150.MirrorCS"),sQuery(id+"F31.wireOp",EDGE,"E163.MirrorCS")])]})});
            var Q17;
            Q17=makeQuery(id+"F32.boolean.opBoolean","COPY",EDGE,{"derivedFrom":makeQuery(id+"F32.opExtrude","SWEPT_EDGE",EDGE,{"disambiguationData":[OSD([sQuery(id+"F31.wireOp",EDGE,"E152.MirrorCS"),sQuery(id+"F31.wireOp",EDGE,"E162.MirrorCS")])]})});
            var Q18;
            Q18=makeQuery(id+"F32.boolean.opBoolean","COPY",EDGE,{"derivedFrom":makeQuery(id+"F32.opExtrude","SWEPT_EDGE",EDGE,{"disambiguationData":[OSD([sQuery(id+"F31.wireOp",EDGE,"E154.MirrorCS"),sQuery(id+"F31.wireOp",EDGE,"E161.MirrorCS")])]})});
            var Q19;
            Q19=makeQuery(id+"F32.boolean.opBoolean","COPY",EDGE,{"derivedFrom":makeQuery(id+"F32.opExtrude","SWEPT_EDGE",EDGE,{"disambiguationData":[OSD([sQuery(id+"F31.wireOp",EDGE,"E156.MirrorCS"),sQuery(id+"F31.wireOp",EDGE,"E158.MirrorCS")])]})});
            var Q20;
            Q20=makeQuery(id+"F32.boolean.opBoolean","COPY",EDGE,{"derivedFrom":makeQuery(id+"F32.opExtrude","SWEPT_EDGE",EDGE,{"disambiguationData":[OSD([sQuery(id+"F31.wireOp",EDGE,"E157.MirrorCS"),sQuery(id+"F31.wireOp",EDGE,"E158.MirrorCS")])]})});
            var Q21;
            Q21=makeQuery(id+"F32.boolean.opBoolean","COPY",EDGE,{"derivedFrom":makeQuery(id+"F32.opExtrude","SWEPT_EDGE",EDGE,{"disambiguationData":[OSD([sQuery(id+"F31.wireOp",EDGE,"E155.MirrorCS"),sQuery(id+"F31.wireOp",EDGE,"E161.MirrorCS")])]})});
            var Q22;
            Q22=makeQuery(id+"F32.boolean.opBoolean","COPY",EDGE,{"derivedFrom":makeQuery(id+"F32.opExtrude","SWEPT_EDGE",EDGE,{"disambiguationData":[OSD([sQuery(id+"F31.wireOp",EDGE,"E153.MirrorCS"),sQuery(id+"F31.wireOp",EDGE,"E162.MirrorCS")])]})});
            var Q23;
            Q23=makeQuery(id+"F32.boolean.opBoolean","COPY",EDGE,{"derivedFrom":makeQuery(id+"F32.opExtrude","SWEPT_EDGE",EDGE,{"disambiguationData":[OSD([sQuery(id+"F31.wireOp",EDGE,"E151.MirrorCS"),sQuery(id+"F31.wireOp",EDGE,"E163.MirrorCS")])]})});
            var Q24;
            Q24=makeQuery(id+"F32.boolean.opBoolean","COPY",EDGE,{"derivedFrom":makeQuery(id+"F32.opExtrude","SWEPT_EDGE",EDGE,{"disambiguationData":[OSD([sQuery(id+"F31.wireOp",EDGE,"E146.MirrorCS"),sQuery(id+"F31.wireOp",EDGE,"E157.MirrorCS")])]})});
            var Q25;
            Q25=makeQuery(id+"F32.boolean.opBoolean","COPY",EDGE,{"derivedFrom":makeQuery(id+"F32.opExtrude","SWEPT_EDGE",EDGE,{"disambiguationData":[OSD([sQuery(id+"F31.wireOp",EDGE,"E147.MirrorCS"),sQuery(id+"F31.wireOp",EDGE,"E155.MirrorCS")])]})});
            var Q26;
            Q26=makeQuery(id+"F32.boolean.opBoolean","COPY",EDGE,{"derivedFrom":makeQuery(id+"F32.opExtrude","SWEPT_EDGE",EDGE,{"disambiguationData":[OSD([sQuery(id+"F31.wireOp",EDGE,"E148.MirrorCS"),sQuery(id+"F31.wireOp",EDGE,"E153.MirrorCS")])]})});
            var Q27;
            Q27=makeQuery(id+"F32.boolean.opBoolean","COPY",EDGE,{"derivedFrom":makeQuery(id+"F32.opExtrude","SWEPT_EDGE",EDGE,{"disambiguationData":[OSD([sQuery(id+"F31.wireOp",EDGE,"E149.MirrorCS"),sQuery(id+"F31.wireOp",EDGE,"E151.MirrorCS")])]})});
            var Q28;
            Q28=makeQuery(id+"F32.boolean.opBoolean","COPY",EDGE,{"derivedFrom":makeQuery(id+"F32.opExtrude","SWEPT_EDGE",EDGE,{"disambiguationData":[OSD([sQuery(id+"F31.wireOp",EDGE,"E146.MirrorCS"),sQuery(id+"F31.wireOp",EDGE,"E156.MirrorCS")])]})});
            var Q29;
            Q29=makeQuery(id+"F32.boolean.opBoolean","COPY",EDGE,{"derivedFrom":makeQuery(id+"F32.opExtrude","SWEPT_EDGE",EDGE,{"disambiguationData":[OSD([sQuery(id+"F31.wireOp",EDGE,"E147.MirrorCS"),sQuery(id+"F31.wireOp",EDGE,"E154.MirrorCS")])]})});
            var Q30;
            Q30=makeQuery(id+"F32.boolean.opBoolean","COPY",EDGE,{"derivedFrom":makeQuery(id+"F32.opExtrude","SWEPT_EDGE",EDGE,{"disambiguationData":[OSD([sQuery(id+"F31.wireOp",EDGE,"E148.MirrorCS"),sQuery(id+"F31.wireOp",EDGE,"E152.MirrorCS")])]})});
            var Q31;
            Q31=makeQuery(id+"F32.boolean.opBoolean","COPY",EDGE,{"derivedFrom":makeQuery(id+"F32.opExtrude","SWEPT_EDGE",EDGE,{"disambiguationData":[OSD([sQuery(id+"F31.wireOp",EDGE,"E149.MirrorCS"),sQuery(id+"F31.wireOp",EDGE,"E150.MirrorCS")])]})});
            var Q32;
            Q32=makeQuery(id+"F34.boolean.opBoolean","COPY",EDGE,{"derivedFrom":makeQuery(id+"F34.opExtrude","SWEPT_EDGE",EDGE,{"disambiguationData":[OSD([sQuery(id+"F33.wireOp",EDGE,"E165.sketch_text.stroke-11"),sQuery(id+"F33.wireOp",EDGE,"E165.sketch_text.stroke-12")])]})});
            var Q33;
            Q33=makeQuery(id+"F34.boolean.opBoolean","COPY",EDGE,{"derivedFrom":makeQuery(id+"F34.opExtrude","SWEPT_EDGE",EDGE,{"disambiguationData":[OSD([sQuery(id+"F33.wireOp",EDGE,"E165.sketch_text.stroke-10"),sQuery(id+"F33.wireOp",EDGE,"E165.sketch_text.stroke-11")])]})});
            var Q34;
            Q34=makeQuery(id+"F34.boolean.opBoolean","COPY",EDGE,{"derivedFrom":makeQuery(id+"F34.opExtrude","SWEPT_EDGE",EDGE,{"disambiguationData":[OSD([sQuery(id+"F33.wireOp",EDGE,"E165.sketch_text.stroke-9"),sQuery(id+"F33.wireOp",EDGE,"E165.sketch_text.stroke-10")])]})});
            var Q35;
            Q35=makeQuery(id+"F34.boolean.opBoolean","COPY",EDGE,{"derivedFrom":makeQuery(id+"F34.opExtrude","SWEPT_EDGE",EDGE,{"disambiguationData":[OSD([sQuery(id+"F33.wireOp",EDGE,"E165.sketch_text.stroke-1"),sQuery(id+"F33.wireOp",EDGE,"E165.sketch_text.stroke-2")])]})});
            var Q36;
            Q36=makeQuery(id+"F34.boolean.opBoolean","COPY",EDGE,{"derivedFrom":makeQuery(id+"F34.opExtrude","SWEPT_EDGE",EDGE,{"disambiguationData":[OSD([sQuery(id+"F33.wireOp",EDGE,"E165.sketch_text.stroke-0"),sQuery(id+"F33.wireOp",EDGE,"E165.sketch_text.stroke-1")])]})});
            var Q37;
            Q37=makeQuery(id+"F34.boolean.opBoolean","COPY",EDGE,{"derivedFrom":makeQuery(id+"F34.opExtrude","SWEPT_EDGE",EDGE,{"disambiguationData":[OSD([sQuery(id+"F33.wireOp",EDGE,"E165.sketch_text.stroke-2"),sQuery(id+"F33.wireOp",EDGE,"E165.sketch_text.stroke-3")])]})});
            var Q38;
            Q38=makeQuery(id+"F34.boolean.opBoolean","COPY",EDGE,{"derivedFrom":makeQuery(id+"F34.opExtrude","SWEPT_EDGE",EDGE,{"disambiguationData":[OSD([sQuery(id+"F33.wireOp",EDGE,"E165.sketch_text.stroke-3"),sQuery(id+"F33.wireOp",EDGE,"E165.sketch_text.stroke-4")])]})});
            fillet(context, id + "F35", {"entities" : qUnion([Q0, Q1, Q2, Q3, Q4, Q5, Q6, Q7, Q8, Q9, Q10, Q11, Q12, Q13, Q14, Q15, Q16, Q17, Q18, Q19, Q20, Q21, Q22, Q23, Q24, Q25, Q26, Q27, Q28, Q29, Q30, Q31, Q32, Q33, Q34, Q35, Q36, Q37, Q38]), "radius" : getVariable(context, 'tool_diameter') / 2, "tangentPropagation" : true, "allowEdgeOverflow" : false});
        }
        {
            var Q0;
            Q0=makeQuery(id+"F30.boolean.opBoolean","COPY",EDGE,{"derivedFrom":makeQuery(id+"F30.opExtrude","SWEPT_EDGE",EDGE,{"disambiguationData":[OSD([sQuery(id+"F27.wireOp",EDGE,"E71.left"),sQuery(id+"F29.wireOp",EDGE,"E79"),sQuery(id+"F29.wireOp",EDGE,"E96")])]})});
            var Q1;
            Q1=makeQuery(id+"F30.boolean.opBoolean","COPY",EDGE,{"derivedFrom":makeQuery(id+"F30.opExtrude","SWEPT_EDGE",EDGE,{"disambiguationData":[OSD([sQuery(id+"F27.wireOp",EDGE,"E71.left"),sQuery(id+"F29.wireOp",EDGE,"E100"),sQuery(id+"F29.wireOp",EDGE,"E101")])]})});
            var Q2;
            Q2=makeQuery(id+"F30.boolean.opBoolean","COPY",EDGE,{"derivedFrom":makeQuery(id+"F30.opExtrude","SWEPT_EDGE",EDGE,{"disambiguationData":[OSD([sQuery(id+"F27.wireOp",EDGE,"E71.left"),sQuery(id+"F29.wireOp",EDGE,"E96"),sQuery(id+"F29.wireOp",EDGE,"E97")])]})});
            var Q3;
            Q3=makeQuery(id+"F30.boolean.opBoolean","COPY",EDGE,{"derivedFrom":makeQuery(id+"F30.opExtrude","SWEPT_EDGE",EDGE,{"disambiguationData":[OSD([sQuery(id+"F27.wireOp",EDGE,"E71.left"),sQuery(id+"F29.wireOp",EDGE,"E81"),sQuery(id+"F29.wireOp",EDGE,"E84")])]})});
            var Q4;
            Q4=makeQuery(id+"F30.boolean.opBoolean","COPY",EDGE,{"derivedFrom":makeQuery(id+"F30.opExtrude","SWEPT_EDGE",EDGE,{"disambiguationData":[OSD([sQuery(id+"F27.wireOp",EDGE,"E71.right"),sQuery(id+"F29.wireOp",EDGE,"E85"),sQuery(id+"F29.wireOp",EDGE,"E88")])]})});
            var Q5;
            Q5=makeQuery(id+"F30.boolean.opBoolean","COPY",EDGE,{"derivedFrom":makeQuery(id+"F30.opExtrude","SWEPT_EDGE",EDGE,{"disambiguationData":[OSD([sQuery(id+"F27.wireOp",EDGE,"E71.right"),sQuery(id+"F29.wireOp",EDGE,"E103"),sQuery(id+"F29.wireOp",EDGE,"E104")])]})});
            var Q6;
            Q6=makeQuery(id+"F30.boolean.opBoolean","COPY",EDGE,{"derivedFrom":makeQuery(id+"F30.opExtrude","SWEPT_EDGE",EDGE,{"disambiguationData":[OSD([sQuery(id+"F27.wireOp",EDGE,"E71.right"),sQuery(id+"F29.wireOp",EDGE,"E94"),sQuery(id+"F29.wireOp",EDGE,"E95")])]})});
            var Q7;
            Q7=makeQuery(id+"F30.boolean.opBoolean","COPY",EDGE,{"derivedFrom":makeQuery(id+"F30.opExtrude","SWEPT_EDGE",EDGE,{"disambiguationData":[OSD([sQuery(id+"F27.wireOp",EDGE,"E71.right"),sQuery(id+"F29.wireOp",EDGE,"E80"),sQuery(id+"F29.wireOp",EDGE,"E95")])]})});
            fillet(context, id + "F36", {"entities" : qUnion([Q0, Q1, Q2, Q3, Q4, Q5, Q6, Q7]), "radius" : getVariable(context, 'tabs_fillet_radius'), "tangentPropagation" : true, "allowEdgeOverflow" : false});
        }
        {
            var Q0;
            Q0=makeQuery(id+"F28.opExtrude","CAP_FACE",FACE,{"disambiguationData":[OSD([sQuery(id+"F27.wireOp",EDGE,"E71.bottom"),sQuery(id+"F27.wireOp",EDGE,"E71.top"),sQuery(id+"F27.wireOp",EDGE,"E71.left"),sQuery(id+"F27.wireOp",EDGE,"E71.right")])],"isStart":true});
            var sketch = newSketch(context, id + "F37", { "sketchPlane" : qUnion([Q0])});
            skArc(sketch, "E168", {"start": v(-106.47, -151.82) * mm, "mid": v(-101.6, -152.4) * mm, "end": v(-101.02, -157.27) * mm});
            skArc(sketch, "E169", {"start": v(-106.47, -151.82) * mm, "mid": v(-107.47, -152.25) * mm, "end": v(-108.54, -152.4) * mm});
            skArc(sketch, "E170", {"start": v(-101.02, -157.27) * mm, "mid": v(-101.45, -158.27) * mm, "end": v(-101.6, -159.34) * mm});
            skLineSegment(sketch, "E171", {"start": v(-108.54, -152.4) * mm, "end": v(-101.6, -159.34) * mm});
            skLineSegment(sketch, "E172", {"start": v(-104.4, -155.2) * mm, "end": v(-101.6, -152.4) * mm, "construction": true});
            skLineSegment(sketch, "E173", {"start": v(-101.6, -190.5) * mm, "end": v(101.6, -190.5) * mm, "construction": true});
            skLineSegment(sketch, "E174.MirrorCS", {"start": v(-108.54, -228.6) * mm, "end": v(-101.6, -221.66) * mm});
            skArc(sketch, "E175.MirrorCS", {"start": v(-106.47, -229.18) * mm, "mid": v(-107.47, -228.75) * mm, "end": v(-108.54, -228.6) * mm});
            skArc(sketch, "E176.MirrorCS", {"start": v(-106.47, -229.18) * mm, "mid": v(-101.6, -228.6) * mm, "end": v(-101.02, -223.73) * mm});
            skArc(sketch, "E177.MirrorCS", {"start": v(-101.02, -223.73) * mm, "mid": v(-101.45, -222.73) * mm, "end": v(-101.6, -221.66) * mm});
            skLineSegment(sketch, "E178", {"start": v(-120.65, -266.7) * mm, "end": v(120.65, -266.7) * mm, "construction": true});
            skLineSegment(sketch, "E179.MirrorCS", {"start": v(-108.54, -304.8) * mm, "end": v(-101.6, -311.74) * mm});
            skArc(sketch, "E180.MirrorCS", {"start": v(-106.47, -304.22) * mm, "mid": v(-107.47, -304.65) * mm, "end": v(-108.54, -304.8) * mm});
            skArc(sketch, "E181.MirrorCS", {"start": v(-106.47, -304.22) * mm, "mid": v(-101.6, -304.8) * mm, "end": v(-101.02, -309.67) * mm});
            skArc(sketch, "E182.MirrorCS", {"start": v(-101.02, -309.67) * mm, "mid": v(-101.45, -310.67) * mm, "end": v(-101.6, -311.74) * mm});
            skLineSegment(sketch, "E183", {"start": v(-118.77, -228.6) * mm, "end": v(-118.77, -457.2) * mm, "construction": true});
            skLineSegment(sketch, "E184", {"start": v(-118.77, -342.9) * mm, "end": v(-101.6, -342.9) * mm, "construction": true});
            skLineSegment(sketch, "E185.MirrorCS", {"start": v(-108.54, -457.2) * mm, "end": v(-101.6, -464.14) * mm});
            skArc(sketch, "E186.MirrorCS", {"start": v(-101.02, -462.07) * mm, "mid": v(-101.45, -463.07) * mm, "end": v(-101.6, -464.14) * mm});
            skArc(sketch, "E187.MirrorCS", {"start": v(-106.47, -456.62) * mm, "mid": v(-101.6, -457.2) * mm, "end": v(-101.02, -462.07) * mm});
            skArc(sketch, "E188.MirrorCS", {"start": v(-106.47, -456.62) * mm, "mid": v(-107.47, -457.05) * mm, "end": v(-108.54, -457.2) * mm});
            skLineSegment(sketch, "E189", {"start": v(0, -19.05) * mm, "end": v(0, -533.4) * mm, "construction": true});
            skArc(sketch, "E190.MirrorCS", {"start": v(106.47, -456.62) * mm, "mid": v(107.47, -457.05) * mm, "end": v(108.54, -457.2) * mm});
            skArc(sketch, "E191.MirrorCS", {"start": v(106.47, -456.62) * mm, "mid": v(101.6, -457.2) * mm, "end": v(101.02, -462.07) * mm});
            skLineSegment(sketch, "E192.MirrorCS", {"start": v(108.54, -457.2) * mm, "end": v(101.6, -464.14) * mm});
            skArc(sketch, "E193.MirrorCS", {"start": v(101.02, -462.07) * mm, "mid": v(101.45, -463.07) * mm, "end": v(101.6, -464.14) * mm});
            skArc(sketch, "E194.MirrorCS", {"start": v(106.47, -304.22) * mm, "mid": v(107.47, -304.65) * mm, "end": v(108.54, -304.8) * mm});
            skArc(sketch, "E195.MirrorCS", {"start": v(106.47, -304.22) * mm, "mid": v(101.6, -304.8) * mm, "end": v(101.02, -309.67) * mm});
            skArc(sketch, "E196.MirrorCS", {"start": v(101.02, -309.67) * mm, "mid": v(101.45, -310.67) * mm, "end": v(101.6, -311.74) * mm});
            skLineSegment(sketch, "E197.MirrorCS", {"start": v(108.54, -304.8) * mm, "end": v(101.6, -311.74) * mm});
            skLineSegment(sketch, "E198.MirrorCS", {"start": v(108.54, -228.6) * mm, "end": v(101.6, -221.66) * mm});
            skArc(sketch, "E199.MirrorCS", {"start": v(106.47, -229.18) * mm, "mid": v(107.47, -228.75) * mm, "end": v(108.54, -228.6) * mm});
            skArc(sketch, "E200.MirrorCS", {"start": v(106.47, -229.18) * mm, "mid": v(101.6, -228.6) * mm, "end": v(101.02, -223.73) * mm});
            skArc(sketch, "E201.MirrorCS", {"start": v(101.02, -223.73) * mm, "mid": v(101.45, -222.73) * mm, "end": v(101.6, -221.66) * mm});
            skArc(sketch, "E202.MirrorCS", {"start": v(106.47, -151.82) * mm, "mid": v(107.47, -152.25) * mm, "end": v(108.54, -152.4) * mm});
            skLineSegment(sketch, "E203.MirrorCS", {"start": v(108.54, -152.4) * mm, "end": v(101.6, -159.34) * mm});
            skArc(sketch, "E204.MirrorCS", {"start": v(106.47, -151.82) * mm, "mid": v(101.6, -152.4) * mm, "end": v(101.02, -157.27) * mm});
            skArc(sketch, "E205.MirrorCS", {"start": v(101.02, -157.27) * mm, "mid": v(101.45, -158.27) * mm, "end": v(101.6, -159.34) * mm});
            skSolve(sketch);
        }
        {
            var Q0;
            Q0 = qSketchRegion(id + "F37", true);
            extrude(context, id + "F38", {"entities" : qUnion([Q0]), "operationType" : NewBodyOperationType.REMOVE, "oppositeDirection" : true, "depth" : getVariable(context, 'material_thickness')});
        }
        {
            var Q0;
            Q0=makeQuery(id+"F9.opExtrude","SWEPT_BODY",BODY,{"disambiguationData":[OSD([sQuery(id+"F8.wireOp",EDGE,"E0.bottom"),sQuery(id+"F8.wireOp",EDGE,"E0.top"),sQuery(id+"F8.wireOp",EDGE,"E0.left"),sQuery(id+"F8.wireOp",EDGE,"E0.right")])]});
            var Q1;
            Q1=qCreatedBy(makeId("Right.planeOp"),FACE);
            mirror(context, id + "F39", {"entities" : qUnion([Q0]), "mirrorPlane" : qUnion([Q1])});
        }
        {
            var Q0;
            Q0=qCreatedBy(makeId("Top.planeOp"),FACE);
            var sketch = newSketch(context, id + "F40", { "sketchPlane" : qUnion([Q0])});
            skLineSegment(sketch, "E206.bottom", {"start": v(-139.7, 387.35) * mm, "end": v(139.7, 387.35) * mm});
            skLineSegment(sketch, "E206.top", {"start": v(-139.7, -19.05) * mm, "end": v(139.7, -19.05) * mm});
            skLineSegment(sketch, "E206.left", {"start": v(-139.7, 387.35) * mm, "end": v(-139.7, -19.05) * mm});
            skLineSegment(sketch, "E206.right", {"start": v(139.7, 387.35) * mm, "end": v(139.7, -19.05) * mm});
            skPoint(sketch, "E207", {"position": v(0, -19.05) * mm});
            skSolve(sketch);
        }
        {
            var Q0;
            Q0 = qSketchRegion(id + "F40", true);
            extrude(context, id + "F41", {"entities" : qUnion([Q0]), "oppositeDirection" : true, "depth" : getVariable(context, 'material_thickness')});
        }
        {
            var Q0;
            Q0=makeQuery(id+"F41.opExtrude","CAP_FACE",FACE,{"disambiguationData":[OSD([sQuery(id+"F40.wireOp",EDGE,"E206.bottom"),sQuery(id+"F40.wireOp",EDGE,"E206.top"),sQuery(id+"F40.wireOp",EDGE,"E206.left"),sQuery(id+"F40.wireOp",EDGE,"E206.right")])],"isStart":true});
            var sketch = newSketch(context, id + "F42", { "sketchPlane" : qUnion([Q0])});
            skLineSegment(sketch, "E208.bottom", {"start": v(-120.9, 368.55) * mm, "end": v(-101.6, 368.55) * mm});
            skLineSegment(sketch, "E208.top", {"start": v(-120.9, 311.15) * mm, "end": v(-101.6, 311.15) * mm});
            skLineSegment(sketch, "E208.left", {"start": v(-120.9, 368.55) * mm, "end": v(-120.9, 311.15) * mm});
            skLineSegment(sketch, "E208.right", {"start": v(-101.6, 368.55) * mm, "end": v(-101.6, 311.15) * mm});
            skLineSegment(sketch, "E209.MirrorCS", {"start": v(120.9, 311.15) * mm, "end": v(101.6, 311.15) * mm});
            skLineSegment(sketch, "E210.MirrorCS", {"start": v(101.6, 368.55) * mm, "end": v(101.6, 311.15) * mm});
            skLineSegment(sketch, "E211.MirrorCS", {"start": v(120.9, 368.55) * mm, "end": v(101.6, 368.55) * mm});
            skLineSegment(sketch, "E212.MirrorCS", {"start": v(120.9, 368.55) * mm, "end": v(120.9, 311.15) * mm});
            skLineSegment(sketch, "E213.bottom", {"start": v(-120.9, 57.15) * mm, "end": v(-101.6, 57.15) * mm});
            skLineSegment(sketch, "E213.top", {"start": v(-120.9, -0.25) * mm, "end": v(-101.6, -0.25) * mm});
            skLineSegment(sketch, "E213.left", {"start": v(-120.9, 57.15) * mm, "end": v(-120.9, -0.25) * mm});
            skLineSegment(sketch, "E213.right", {"start": v(-101.6, 57.15) * mm, "end": v(-101.6, -0.25) * mm});
            skLineSegment(sketch, "E214.MirrorCS", {"start": v(120.9, -0.25) * mm, "end": v(101.6, -0.25) * mm});
            skLineSegment(sketch, "E215.MirrorCS", {"start": v(101.6, 57.15) * mm, "end": v(101.6, -0.25) * mm});
            skLineSegment(sketch, "E216.MirrorCS", {"start": v(120.9, 57.15) * mm, "end": v(101.6, 57.15) * mm});
            skLineSegment(sketch, "E217.MirrorCS", {"start": v(120.9, 57.15) * mm, "end": v(120.9, -0.25) * mm});
            skSolve(sketch);
        }
        {
            var Q0;
            Q0 = qSketchRegion(id + "F42", true);
            extrude(context, id + "F43", {"entities" : qUnion([Q0]), "operationType" : NewBodyOperationType.REMOVE, "oppositeDirection" : true, "depth" : getVariable(context, 'material_thickness')});
        }
        {
            var Q0;
            Q0=makeQuery(id+"F41.opExtrude","CAP_FACE",FACE,{"disambiguationData":[OSD([sQuery(id+"F40.wireOp",EDGE,"E206.bottom"),sQuery(id+"F40.wireOp",EDGE,"E206.top"),sQuery(id+"F40.wireOp",EDGE,"E206.left"),sQuery(id+"F40.wireOp",EDGE,"E206.right")])],"isStart":true});
            var sketch = newSketch(context, id + "F44", { "sketchPlane" : qUnion([Q0])});
            skArc(sketch, "E218", {"start": v(-121.49, 363.68) * mm, "mid": v(-120.9, 368.55) * mm, "end": v(-116.03, 369.14) * mm});
            skArc(sketch, "E219", {"start": v(-116.03, 369.14) * mm, "mid": v(-115.04, 368.7) * mm, "end": v(-113.96, 368.55) * mm});
            skArc(sketch, "E220", {"start": v(-121.49, 363.68) * mm, "mid": v(-121.05, 362.69) * mm, "end": v(-120.9, 361.61) * mm});
            skLineSegment(sketch, "E221", {"start": v(-120.9, 368.55) * mm, "end": v(-118.1, 365.75) * mm, "construction": true});
            skLineSegment(sketch, "E222", {"start": v(-120.9, 361.61) * mm, "end": v(-113.96, 368.55) * mm});
            skLineSegment(sketch, "E223", {"start": v(-111.25, 368.55) * mm, "end": v(-111.25, 311.15) * mm, "construction": true});
            skLineSegment(sketch, "E224", {"start": v(-120.9, 339.85) * mm, "end": v(-101.6, 339.85) * mm, "construction": true});
            skArc(sketch, "E225.MirrorCS", {"start": v(-101.02, 363.68) * mm, "mid": v(-101.45, 362.69) * mm, "end": v(-101.6, 361.61) * mm});
            skArc(sketch, "E226.MirrorCS", {"start": v(-106.47, 369.14) * mm, "mid": v(-107.47, 368.7) * mm, "end": v(-108.54, 368.55) * mm});
            skLineSegment(sketch, "E227.MirrorCS", {"start": v(-101.6, 368.55) * mm, "end": v(-104.4, 365.75) * mm, "construction": true});
            skArc(sketch, "E228.MirrorCS", {"start": v(-101.02, 363.68) * mm, "mid": v(-101.6, 368.55) * mm, "end": v(-106.47, 369.14) * mm});
            skLineSegment(sketch, "E229.MirrorCS", {"start": v(-101.6, 361.61) * mm, "end": v(-108.54, 368.55) * mm});
            skArc(sketch, "E230.MirrorCS", {"start": v(-116.03, 310.57) * mm, "mid": v(-115.04, 311) * mm, "end": v(-113.96, 311.15) * mm});
            skArc(sketch, "E231.MirrorCS", {"start": v(-121.49, 316.02) * mm, "mid": v(-121.05, 317.02) * mm, "end": v(-120.9, 318.1) * mm});
            skArc(sketch, "E232.MirrorCS", {"start": v(-101.02, 316.02) * mm, "mid": v(-101.45, 317.02) * mm, "end": v(-101.6, 318.1) * mm});
            skArc(sketch, "E233.MirrorCS", {"start": v(-106.47, 310.57) * mm, "mid": v(-107.47, 311) * mm, "end": v(-108.54, 311.15) * mm});
            skLineSegment(sketch, "E234.MirrorCS", {"start": v(-101.6, 311.15) * mm, "end": v(-104.4, 313.96) * mm, "construction": true});
            skArc(sketch, "E235.MirrorCS", {"start": v(-121.49, 316.02) * mm, "mid": v(-120.9, 311.15) * mm, "end": v(-116.03, 310.57) * mm});
            skLineSegment(sketch, "E236.MirrorCS", {"start": v(-101.6, 318.1) * mm, "end": v(-108.54, 311.15) * mm});
            skLineSegment(sketch, "E237.MirrorCS", {"start": v(-120.9, 311.15) * mm, "end": v(-118.1, 313.96) * mm, "construction": true});
            skLineSegment(sketch, "E238.MirrorCS", {"start": v(-120.9, 318.1) * mm, "end": v(-113.96, 311.15) * mm});
            skArc(sketch, "E239.MirrorCS", {"start": v(-101.02, 316.02) * mm, "mid": v(-101.6, 311.15) * mm, "end": v(-106.47, 310.57) * mm});
            skLineSegment(sketch, "E240.MirrorCS", {"start": v(-111.25, 311.15) * mm, "end": v(-111.25, 368.55) * mm, "construction": true});
            skLineSegment(sketch, "E241", {"start": v(-101.6, 339.85) * mm, "end": v(101.6, 339.85) * mm, "construction": true});
            skLineSegment(sketch, "E242", {"start": v(-101.6, 28.45) * mm, "end": v(101.6, 28.45) * mm, "construction": true});
            skLineSegment(sketch, "E243", {"start": v(111.25, 57.15) * mm, "end": v(111.25, 311.15) * mm, "construction": true});
            skLineSegment(sketch, "E244", {"start": v(-111.25, 311.15) * mm, "end": v(-111.25, 57.15) * mm, "construction": true});
            skLineSegment(sketch, "E245", {"start": v(0, 339.85) * mm, "end": v(0, 28.45) * mm, "construction": true});
            skLineSegment(sketch, "E246", {"start": v(-111.25, 184.15) * mm, "end": v(111.25, 184.15) * mm, "construction": true});
            skArc(sketch, "E247.MirrorCS", {"start": v(116.03, 369.14) * mm, "mid": v(115.04, 368.7) * mm, "end": v(113.96, 368.55) * mm});
            skArc(sketch, "E248.MirrorCS", {"start": v(121.49, 363.68) * mm, "mid": v(121.05, 362.69) * mm, "end": v(120.9, 361.61) * mm});
            skLineSegment(sketch, "E249.MirrorCS", {"start": v(120.9, 318.1) * mm, "end": v(113.96, 311.15) * mm});
            skArc(sketch, "E250.MirrorCS", {"start": v(106.47, 310.57) * mm, "mid": v(107.47, 311) * mm, "end": v(108.54, 311.15) * mm});
            skArc(sketch, "E251.MirrorCS", {"start": v(121.49, 316.02) * mm, "mid": v(120.9, 311.15) * mm, "end": v(116.03, 310.57) * mm});
            skLineSegment(sketch, "E252.MirrorCS", {"start": v(120.9, 361.61) * mm, "end": v(113.96, 368.55) * mm});
            skLineSegment(sketch, "E253.MirrorCS", {"start": v(120.9, 368.55) * mm, "end": v(118.1, 365.75) * mm, "construction": true});
            skLineSegment(sketch, "E254.MirrorCS", {"start": v(120.9, 311.15) * mm, "end": v(118.1, 313.96) * mm, "construction": true});
            skArc(sketch, "E255.MirrorCS", {"start": v(121.49, 316.02) * mm, "mid": v(121.05, 317.02) * mm, "end": v(120.9, 318.1) * mm});
            skArc(sketch, "E256.MirrorCS", {"start": v(116.03, 310.57) * mm, "mid": v(115.04, 311) * mm, "end": v(113.96, 311.15) * mm});
            skArc(sketch, "E257.MirrorCS", {"start": v(121.49, 363.68) * mm, "mid": v(120.9, 368.55) * mm, "end": v(116.03, 369.14) * mm});
            skLineSegment(sketch, "E258.MirrorCS", {"start": v(101.6, 361.61) * mm, "end": v(108.54, 368.55) * mm});
            skLineSegment(sketch, "E259.MirrorCS", {"start": v(101.6, 368.55) * mm, "end": v(104.4, 365.75) * mm, "construction": true});
            skLineSegment(sketch, "E260.MirrorCS", {"start": v(101.6, 318.1) * mm, "end": v(108.54, 311.15) * mm});
            skLineSegment(sketch, "E261.MirrorCS", {"start": v(101.6, 311.15) * mm, "end": v(104.4, 313.96) * mm, "construction": true});
            skArc(sketch, "E262.MirrorCS", {"start": v(106.47, 369.14) * mm, "mid": v(107.47, 368.7) * mm, "end": v(108.54, 368.55) * mm});
            skArc(sketch, "E263.MirrorCS", {"start": v(101.02, 316.02) * mm, "mid": v(101.6, 311.15) * mm, "end": v(106.47, 310.57) * mm});
            skArc(sketch, "E264.MirrorCS", {"start": v(101.02, 316.02) * mm, "mid": v(101.45, 317.02) * mm, "end": v(101.6, 318.1) * mm});
            skArc(sketch, "E265.MirrorCS", {"start": v(101.02, 363.68) * mm, "mid": v(101.6, 368.55) * mm, "end": v(106.47, 369.14) * mm});
            skArc(sketch, "E266.MirrorCS", {"start": v(101.02, 363.68) * mm, "mid": v(101.45, 362.69) * mm, "end": v(101.6, 361.61) * mm});
            skLineSegment(sketch, "E267.MirrorCS", {"start": v(111.25, 311.15) * mm, "end": v(111.25, 368.55) * mm, "construction": true});
            skLineSegment(sketch, "E268.MirrorCS", {"start": v(120.9, 339.85) * mm, "end": v(101.6, 339.85) * mm, "construction": true});
            skLineSegment(sketch, "E269.MirrorCS", {"start": v(111.25, 368.55) * mm, "end": v(111.25, 311.15) * mm, "construction": true});
            skLineSegment(sketch, "E270.MirrorCS", {"start": v(-120.9, 57.15) * mm, "end": v(-118.1, 54.34) * mm, "construction": true});
            skArc(sketch, "E271.MirrorCS", {"start": v(-116.03, 57.73) * mm, "mid": v(-115.04, 57.3) * mm, "end": v(-113.96, 57.15) * mm});
            skArc(sketch, "E272.MirrorCS", {"start": v(-106.47, 57.73) * mm, "mid": v(-107.47, 57.3) * mm, "end": v(-108.54, 57.15) * mm});
            skArc(sketch, "E273.MirrorCS", {"start": v(-121.49, 4.62) * mm, "mid": v(-121.05, 5.61) * mm, "end": v(-120.9, 6.69) * mm});
            skArc(sketch, "E274.MirrorCS", {"start": v(-116.03, -0.84) * mm, "mid": v(-115.04, -0.4) * mm, "end": v(-113.96, -0.25) * mm});
            skArc(sketch, "E275.MirrorCS", {"start": v(-121.49, 4.62) * mm, "mid": v(-120.9, -0.25) * mm, "end": v(-116.03, -0.84) * mm});
            skLineSegment(sketch, "E276.MirrorCS", {"start": v(-101.6, 50.2) * mm, "end": v(-108.54, 57.15) * mm});
            skLineSegment(sketch, "E277.MirrorCS", {"start": v(-120.9, 50.2) * mm, "end": v(-113.96, 57.15) * mm});
            skArc(sketch, "E278.MirrorCS", {"start": v(-106.47, -0.84) * mm, "mid": v(-107.47, -0.4) * mm, "end": v(-108.54, -0.25) * mm});
            skLineSegment(sketch, "E279.MirrorCS", {"start": v(-101.6, -0.25) * mm, "end": v(-104.4, 2.55) * mm, "construction": true});
            skLineSegment(sketch, "E280.MirrorCS", {"start": v(-120.9, -0.25) * mm, "end": v(-118.1, 2.55) * mm, "construction": true});
            skLineSegment(sketch, "E281.MirrorCS", {"start": v(-120.9, 6.69) * mm, "end": v(-113.96, -0.25) * mm});
            skLineSegment(sketch, "E282.MirrorCS", {"start": v(-101.6, 6.69) * mm, "end": v(-108.54, -0.25) * mm});
            skArc(sketch, "E283.MirrorCS", {"start": v(-101.02, 52.28) * mm, "mid": v(-101.6, 57.15) * mm, "end": v(-106.47, 57.73) * mm});
            skArc(sketch, "E284.MirrorCS", {"start": v(-101.02, 4.62) * mm, "mid": v(-101.45, 5.61) * mm, "end": v(-101.6, 6.69) * mm});
            skLineSegment(sketch, "E285.MirrorCS", {"start": v(-101.6, 57.15) * mm, "end": v(-104.4, 54.34) * mm, "construction": true});
            skArc(sketch, "E286.MirrorCS", {"start": v(-121.49, 52.28) * mm, "mid": v(-120.9, 57.15) * mm, "end": v(-116.03, 57.73) * mm});
            skArc(sketch, "E287.MirrorCS", {"start": v(-101.02, 52.28) * mm, "mid": v(-101.45, 51.28) * mm, "end": v(-101.6, 50.2) * mm});
            skArc(sketch, "E288.MirrorCS", {"start": v(-101.02, 4.62) * mm, "mid": v(-101.6, -0.25) * mm, "end": v(-106.47, -0.84) * mm});
            skArc(sketch, "E289.MirrorCS", {"start": v(-121.49, 52.28) * mm, "mid": v(-121.05, 51.28) * mm, "end": v(-120.9, 50.2) * mm});
            skLineSegment(sketch, "E290.MirrorCS", {"start": v(-111.25, 57.15) * mm, "end": v(-111.25, -0.25) * mm, "construction": true});
            skLineSegment(sketch, "E291.MirrorCS", {"start": v(-111.25, -0.25) * mm, "end": v(-111.25, 57.15) * mm, "construction": true});
            skLineSegment(sketch, "E292.MirrorCS", {"start": v(-120.9, 28.45) * mm, "end": v(-101.6, 28.45) * mm, "construction": true});
            skArc(sketch, "E293.MirrorCS", {"start": v(116.03, -0.84) * mm, "mid": v(115.04, -0.4) * mm, "end": v(113.96, -0.25) * mm});
            skLineSegment(sketch, "E294.MirrorCS", {"start": v(101.6, 50.2) * mm, "end": v(108.54, 57.15) * mm});
            skArc(sketch, "E295.MirrorCS", {"start": v(106.47, -0.84) * mm, "mid": v(107.47, -0.4) * mm, "end": v(108.54, -0.25) * mm});
            skArc(sketch, "E296.MirrorCS", {"start": v(116.03, 57.73) * mm, "mid": v(115.04, 57.3) * mm, "end": v(113.96, 57.15) * mm});
            skArc(sketch, "E297.MirrorCS", {"start": v(106.47, 57.73) * mm, "mid": v(107.47, 57.3) * mm, "end": v(108.54, 57.15) * mm});
            skLineSegment(sketch, "E298.MirrorCS", {"start": v(120.9, 6.69) * mm, "end": v(113.96, -0.25) * mm});
            skLineSegment(sketch, "E299.MirrorCS", {"start": v(120.9, -0.25) * mm, "end": v(118.1, 2.55) * mm, "construction": true});
            skArc(sketch, "E300.MirrorCS", {"start": v(101.02, 52.28) * mm, "mid": v(101.45, 51.28) * mm, "end": v(101.6, 50.2) * mm});
            skArc(sketch, "E301.MirrorCS", {"start": v(101.02, 52.28) * mm, "mid": v(101.6, 57.15) * mm, "end": v(106.47, 57.73) * mm});
            skArc(sketch, "E302.MirrorCS", {"start": v(121.49, 52.28) * mm, "mid": v(121.05, 51.28) * mm, "end": v(120.9, 50.2) * mm});
            skLineSegment(sketch, "E303.MirrorCS", {"start": v(101.6, 57.15) * mm, "end": v(104.4, 54.34) * mm, "construction": true});
            skLineSegment(sketch, "E304.MirrorCS", {"start": v(101.6, -0.25) * mm, "end": v(104.4, 2.55) * mm, "construction": true});
            skLineSegment(sketch, "E305.MirrorCS", {"start": v(120.9, 50.2) * mm, "end": v(113.96, 57.15) * mm});
            skLineSegment(sketch, "E306.MirrorCS", {"start": v(120.9, 57.15) * mm, "end": v(118.1, 54.34) * mm, "construction": true});
            skArc(sketch, "E307.MirrorCS", {"start": v(121.49, 4.62) * mm, "mid": v(121.05, 5.61) * mm, "end": v(120.9, 6.69) * mm});
            skLineSegment(sketch, "E308.MirrorCS", {"start": v(101.6, 6.69) * mm, "end": v(108.54, -0.25) * mm});
            skArc(sketch, "E309.MirrorCS", {"start": v(121.49, 52.28) * mm, "mid": v(120.9, 57.15) * mm, "end": v(116.03, 57.73) * mm});
            skArc(sketch, "E310.MirrorCS", {"start": v(121.49, 4.62) * mm, "mid": v(120.9, -0.25) * mm, "end": v(116.03, -0.84) * mm});
            skArc(sketch, "E311.MirrorCS", {"start": v(101.02, 4.62) * mm, "mid": v(101.6, -0.25) * mm, "end": v(106.47, -0.84) * mm});
            skArc(sketch, "E312.MirrorCS", {"start": v(101.02, 4.62) * mm, "mid": v(101.45, 5.61) * mm, "end": v(101.6, 6.69) * mm});
            skLineSegment(sketch, "E313.MirrorCS", {"start": v(120.9, 28.45) * mm, "end": v(101.6, 28.45) * mm, "construction": true});
            skLineSegment(sketch, "E314.MirrorCS", {"start": v(111.25, -0.25) * mm, "end": v(111.25, 57.15) * mm, "construction": true});
            skLineSegment(sketch, "E315.MirrorCS", {"start": v(111.25, 311.15) * mm, "end": v(111.25, 57.15) * mm, "construction": true});
            skLineSegment(sketch, "E316.MirrorCS", {"start": v(111.25, 57.15) * mm, "end": v(111.25, -0.25) * mm, "construction": true});
            skSolve(sketch);
        }
        {
            var Q0;
            Q0 = qSketchRegion(id + "F44", true);
            extrude(context, id + "F45", {"entities" : qUnion([Q0]), "operationType" : NewBodyOperationType.REMOVE, "oppositeDirection" : true, "depth" : getVariable(context, 'material_thickness')});
        }
        {
            var Q0;
            Q0=makeQuery(id+"F41.opExtrude","SWEPT_EDGE",EDGE,{"disambiguationData":[OSD([sQuery(id+"F40.wireOp",EDGE,"E206.bottom"),sQuery(id+"F40.wireOp",EDGE,"E206.left")])]});
            var Q1;
            Q1=makeQuery(id+"F41.opExtrude","SWEPT_EDGE",EDGE,{"disambiguationData":[OSD([sQuery(id+"F40.wireOp",EDGE,"E206.top"),sQuery(id+"F40.wireOp",EDGE,"E206.left")])]});
            var Q2;
            Q2=makeQuery(id+"F41.opExtrude","SWEPT_EDGE",EDGE,{"disambiguationData":[OSD([sQuery(id+"F40.wireOp",EDGE,"E206.top"),sQuery(id+"F40.wireOp",EDGE,"E206.right")])]});
            var Q3;
            Q3=makeQuery(id+"F41.opExtrude","SWEPT_EDGE",EDGE,{"disambiguationData":[OSD([sQuery(id+"F40.wireOp",EDGE,"E206.bottom"),sQuery(id+"F40.wireOp",EDGE,"E206.right")])]});
            fillet(context, id + "F46", {"entities" : qUnion([Q0, Q1, Q2, Q3]), "radius" : getVariable(context, 'large_fillet_radius'), "tangentPropagation" : true, "allowEdgeOverflow" : false});
        }
    });
